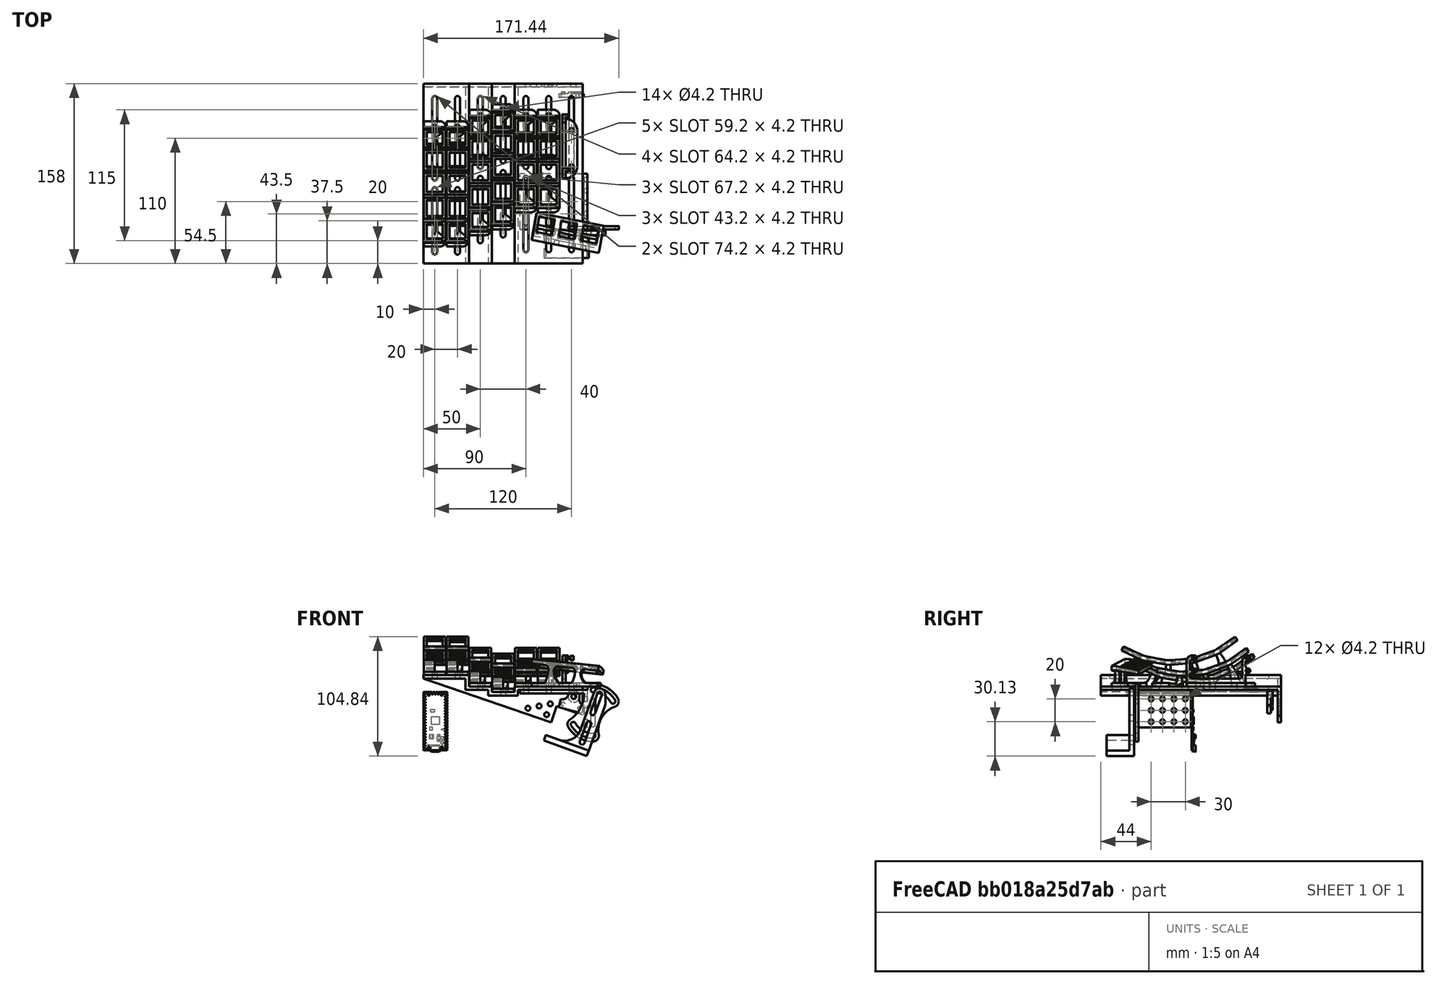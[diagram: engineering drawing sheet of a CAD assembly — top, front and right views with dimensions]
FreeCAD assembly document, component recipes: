
FREECAD ASSEMBLY — COMPONENT RECIPES ("Dactyl Chimera V3")

This assembly document has 15 components, labeled P0..P14 below (a component is one placed body or linked part). 14 of them carry a construction recipe — the FreeCAD feature program that regenerates the part from scratch, quoted from this document or its linked companion documents; the rest are supplied as boundary geometry only. No exploded tour is included for this assembly.
NOTE — document 4 of 4 of this assembly tour. The two overview renders and the header above are repeated from document 1; the component sections below continue where the previous document stopped.
COMPONENT P7 — recipe-attached ("Thumb Cluster", modeled in this document).
Construction recipe (the document's own serialized feature program — sketch geometry with constraints, then the solid features built on it; lengths are millimeters unless a unit is written):

FEATURE [Sketcher::SketchObject] Sketch040
  FullyConstrained = true
  MapMode = 5
  Support = -> [XY_Plane010]
  expr: Constraints[34] = <<Spreadsheet>>.NutR
  expr: Constraints[35] = <<Spreadsheet>>.NutR
  expr: Constraints[41] = <<Spreadsheet>>.NutR
  expr: Constraints[71] = <<Spreadsheet>>.ScrewD
  expr: Constraints[74] = <<Spreadsheet>>.NutR
  sketch-geometry (29):
    g0: LineSegment StartX=-29.5 StartY=10 StartZ=0 EndX=29.5 EndY=10 EndZ=0
    g1: LineSegment StartX=29.5 StartY=10 StartZ=0 EndX=29.5 EndY=0 EndZ=0
    g2: LineSegment StartX=29.5 StartY=0 StartZ=0 EndX=-29.5 EndY=0 EndZ=0
    g3: LineSegment StartX=-29.5 StartY=0 StartZ=0 EndX=-29.5 EndY=10 EndZ=0
    g4: LineSegment StartX=-26.6 StartY=5 StartZ=0 EndX=-26.6 EndY=7.1 EndZ=0
    g5: LineSegment StartX=-26.6 StartY=7.1 StartZ=0 EndX=-10.8667 EndY=7.1 EndZ=0
    g6: LineSegment StartX=-10.8667 StartY=7.1 StartZ=0 EndX=-10.8667 EndY=5 EndZ=0
    g7: LineSegment StartX=-12.9667 StartY=2.9 StartZ=0 EndX=-24.5 EndY=2.9 EndZ=0
    g8: GeomPoint X=-24.5 Y=5 Z=0
    g9: LineSegment StartX=-7.86667 StartY=5 StartZ=0 EndX=-7.86667 EndY=7.1 EndZ=0
    g10: LineSegment StartX=-7.86667 StartY=7.1 StartZ=0 EndX=7.86667 EndY=7.1 EndZ=0
    g11: LineSegment StartX=7.86667 StartY=7.1 StartZ=0 EndX=7.86667 EndY=5 EndZ=0
    g12: LineSegment StartX=5.76667 StartY=2.9 StartZ=0 EndX=-5.76667 EndY=2.9 EndZ=0
    g13: GeomPoint X=0 Y=5 Z=0
    g14: LineSegment StartX=10.8667 StartY=5 StartZ=0 EndX=10.8667 EndY=7.1 EndZ=0
    g15: LineSegment StartX=10.8667 StartY=7.1 StartZ=0 EndX=26.6 EndY=7.1 EndZ=0
    g16: LineSegment StartX=26.6 StartY=7.1 StartZ=0 EndX=26.6 EndY=5 EndZ=0
    g17: LineSegment StartX=24.5 StartY=2.9 StartZ=0 EndX=12.9667 EndY=2.9 EndZ=0
    g18: GeomPoint X=24.5 Y=5 Z=0
    g19: LineSegment StartX=-24.5 StartY=5 StartZ=0 EndX=0 EndY=5 EndZ=0
    g20: LineSegment StartX=0 StartY=5 StartZ=0 EndX=24.5 EndY=5 EndZ=0
    g21: LineSegment StartX=24.5 StartY=2.9 StartZ=0 EndX=26.6 EndY=2.9 EndZ=0
    g22: LineSegment StartX=26.6 StartY=2.9 StartZ=0 EndX=26.6 EndY=5 EndZ=0
    g23: ArcOfCircle CenterX=24.5 CenterY=5 CenterZ=0 NormalX=0 NormalY=0 NormalZ=1 AngleXU=0 Radius=2.1 StartAngle=4.71239 EndAngle=6.28319
    g24: ArcOfCircle CenterX=12.9667 CenterY=5 CenterZ=0 NormalX=0 NormalY=0 NormalZ=1 AngleXU=0 Radius=2.1 StartAngle=3.14159 EndAngle=4.71239
    g25: ArcOfCircle CenterX=5.76667 CenterY=5 CenterZ=0 NormalX=0 NormalY=0 NormalZ=1 AngleXU=0 Radius=2.1 StartAngle=4.71239 EndAngle=6.28319
    g26: ArcOfCircle CenterX=-5.76667 CenterY=5 CenterZ=0 NormalX=0 NormalY=0 NormalZ=1 AngleXU=0 Radius=2.1 StartAngle=3.14159 EndAngle=4.71239
    g27: ArcOfCircle CenterX=-12.9667 CenterY=5 CenterZ=0 NormalX=0 NormalY=0 NormalZ=1 AngleXU=0 Radius=2.1 StartAngle=4.71239 EndAngle=6.28319
    g28: ArcOfCircle CenterX=-24.5 CenterY=5 CenterZ=0 NormalX=0 NormalY=0 NormalZ=1 AngleXU=0 Radius=2.1 StartAngle=3.14159 EndAngle=4.71239
  constraints (76):
    c: Coincident(g0,g1)
    c: Coincident(g1,g2)
    c: Coincident(g2,g3)
    c: Coincident(g3,g0)
    c: Horizontal(g2)
    c: Vertical(g1)
    c: Vertical(g3)
    c: Coincident(g4,g5)
    c: Coincident(g5,g6)
    c: Horizontal(g5)
    c: Horizontal(g7)
    c: Vertical(g4)
    c: Vertical(g6)
    c: Coincident(g9,g10)
    c: Coincident(g10,g11)
    c: Horizontal(g10)
    c: Horizontal(g12)
    c: Vertical(g9)
    c: Vertical(g11)
    c: PointOnObject(g13,g-2)
    c: Coincident(g14,g15)
    c: Coincident(g15,g16)
    c: Horizontal(g15)
    c: Horizontal(g17)
    c: Vertical(g14)
    c: Vertical(g16)
    c: Coincident(g19,g8)
    c: Coincident(g19,g13)
    c: Horizontal(g19)
    c: Coincident(g20,g13)
    c: Coincident(g20,g18)
    c: Horizontal(g20)
    c: Equal(g14,g11)
    c: Equal(g9,g6)
    c: DistanceY(g8,g0) = 5
    c: DistanceY(g2,g8) = 5
    c: DistanceX(g6,g9) = 3
    c: DistanceX(g11,g14) = 3
    c: DistanceX(g2,g2) = 59
    c: Equal(g5,g10)
    c: Equal(g15,g10)
    c: DistanceX(g23,g1) = 5
    c: Symmetric(g0,g0,g-2)
    c: PointOnObject(g-1,g2)
    c: PointOnObject(g14,g20)
    c: PointOnObject(g11,g20)
    c: PointOnObject(g6,g19)
    c: PointOnObject(g9,g19)
    c: PointOnObject(g4,g19)
    c: Coincident(g17,g21)
    c: Coincident(g21,g22)
    c: Coincident(g22,g16)
    c: Vertical(g22)
    c: Tangent(g23,g17) = 1.5708
    c: Tangent(g23,g16) = 1.5708
    c: PointOnObject(g25,g20)
    c: Coincident(g25,g11)
    c: PointOnObject(g26,g19)
    c: Coincident(g26,g9)
    c: PointOnObject(g27,g19)
    c: Coincident(g27,g6)
    c: Coincident(g28,g8)
    c: Coincident(g28,g4)
    c: Tangent(g28,g7) = 1.5708
    c: Tangent(g27,g7) = 1.5708
    c: Tangent(g26,g12) = 1.5708
    c: Tangent(g25,g12) = 1.5708
    c: Tangent(g24,g17) = 1.5708
    c: Tangent(g24,g14) = 1.5708
    c: Coincident(g18,g23)
    c: Equal(g7,g12)
    c: DistanceY(g21,g15) = 4.2
    c: Horizontal(g21)
    c: Equal(g22,g16)
    c: DistanceX(g2,g28) = 5
    c: Horizontal(g17,g12)
FEATURE [PartDesign::Pad] Pad026
  Direction = (0,0,1)
  Length = 3
  Length2 = 10
  Profile = -> Sketch040
  ReferenceAxis = -> Sketch040 [N_Axis]
  Type = 0
FEATURE [PartDesign::Line] DatumLine
  AttacherType = Attacher::AttachEngineLine
  AttachmentOffset = pos=(21,0,0) rot=(0,-1,0;0.10472rad)
  Length = 20
  MapMode = 16
  Placement = pos=(4.7e-15,-4.7e-15,21) rot=(0.743145,0,0.669131;3.14159rad)
  ResizeMode = 0
  Support = -> [XZ_Plane010]
FEATURE [Sketcher::SketchObject] Sketch041
  ExternalGeometry = -> [Sketch040,DatumLine]
  FullyConstrained = true
  MapMode = 5
  Placement = pos=(0,0,0) rot=(1,0,0;1.5708rad)
  Support = -> [XZ_Plane010]
  sketch-geometry (30):
    g0: LineSegment StartX=29.5 StartY=0 StartZ=0 EndX=29.5 EndY=3 EndZ=0
    g1: LineSegment StartX=29.5 StartY=3 StartZ=0 EndX=17.9014 EndY=3 EndZ=0
    g2: LineSegment StartX=-29.5 StartY=0 StartZ=0 EndX=-29.5 EndY=3 EndZ=0
    g3: LineSegment StartX=-29.5 StartY=3 StartZ=0 EndX=-17.9014 EndY=3 EndZ=0
    g4: ArcOfCircle CenterX=-56.761 CenterY=19.4384 CenterZ=0 NormalX=0 NormalY=0 NormalZ=1 AngleXU=0 Radius=42.1934 StartAngle=5.88299 EndAngle=6.17847
    g5: ArcOfCircle CenterX=-14.7725 CenterY=15.0252 CenterZ=0 NormalX=0 NormalY=0 NormalZ=1 AngleXU=0 Radius=23.9737 StartAngle=5.75774 EndAngle=6.17847
    g6: ArcOfCircle CenterX=4.78187 CenterY=12.9699 CenterZ=0 NormalX=0 NormalY=0 NormalZ=1 AngleXU=0 Radius=14.6609 StartAngle=3.03687 EndAngle=3.88941
    g7: ArcOfCircle CenterX=5.60272 CenterY=12.8837 CenterZ=0 NormalX=0 NormalY=0 NormalZ=1 AngleXU=0 Radius=3.48623 StartAngle=6.17847 EndAngle=7.74926
    g8: ArcOfCircle CenterX=-6.33154 CenterY=14.138 CenterZ=0 NormalX=0 NormalY=0 NormalZ=1 AngleXU=0 Radius=3.48623 StartAngle=1.46608 EndAngle=3.03687
    g9: ArcOfCircle CenterX=-18.2658 CenterY=15.3923 CenterZ=0 NormalX=0 NormalY=0 NormalZ=1 AngleXU=0 Radius=3.48623 StartAngle=6.17847 EndAngle=7.74926
    g10: ArcOfCircle CenterX=17.537 CenterY=11.6293 CenterZ=0 NormalX=0 NormalY=0 NormalZ=1 AngleXU=0 Radius=3.48623 StartAngle=1.46608 EndAngle=3.03687
    g11: LineSegment StartX=30.2538 StartY=17.8202 StartZ=0 EndX=-29.4175 EndY=24.0919 EndZ=0
    g12: LineSegment StartX=-29.4175 StartY=24.0919 StartZ=0 EndX=-29.8357 EndY=20.1138 EndZ=0
    g13: LineSegment StartX=-29.8357 StartY=20.1138 StartZ=0 EndX=-17.9014 EndY=18.8595 EndZ=0
    g14: LineSegment StartX=-5.96713 StartY=17.6051 StartZ=0 EndX=5.96713 EndY=16.3508 EndZ=0
    g15: LineSegment StartX=-5.96713 StartY=3 StartZ=0 EndX=5.96713 EndY=3 EndZ=0
    g16: LineSegment StartX=-17.9014 StartY=3 StartZ=0 EndX=-5.96713 EndY=3 EndZ=0
    g17: LineSegment StartX=5.96713 StartY=3 StartZ=0 EndX=17.9014 EndY=3 EndZ=0
    g18: LineSegment StartX=17.9014 StartY=15.0965 StartZ=0 EndX=5.96713 EndY=16.3508 EndZ=0
    g19: LineSegment StartX=-5.96713 StartY=17.6051 StartZ=0 EndX=-17.9014 EndY=18.8595 EndZ=0
    g20: LineSegment StartX=17.9014 StartY=3 StartZ=0 EndX=17.9014 EndY=15.0965 EndZ=0
    g21: LineSegment StartX=5.96713 StartY=3 StartZ=0 EndX=5.96713 EndY=16.3508 EndZ=0
    g22: LineSegment StartX=-5.96713 StartY=17.6051 StartZ=0 EndX=-5.96713 EndY=3 EndZ=0
    g23: LineSegment StartX=-17.9014 StartY=3 StartZ=0 EndX=-17.9014 EndY=18.8595 EndZ=0
    g24: LineSegment StartX=29.5 StartY=0 StartZ=0 EndX=-29.5 EndY=0 EndZ=0
    g25: LineSegment StartX=17.9014 StartY=15.0965 StartZ=0 EndX=29.8357 EndY=13.8421 EndZ=0
    g26: LineSegment StartX=-14.7987 StartY=15.0279 StartZ=0 EndX=14.0699 EndY=11.9937 EndZ=0
    g27: ArcOfCircle CenterX=24.0732 CenterY=10.9423 CenterZ=0 NormalX=0 NormalY=0 NormalZ=1 AngleXU=0 Radius=10.0584 StartAngle=3.03687 EndAngle=4.05179
    g28: LineSegment StartX=29.8357 StartY=13.8421 StartZ=0 EndX=30.2538 EndY=17.8202 EndZ=0
    g29: LineSegment StartX=29.8357 StartY=13.8421 StartZ=0 EndX=28.3808 EndY=0 EndZ=0
  constraints (78):
    c: Coincident(g-3,g0)
    c: Coincident(g0,g1)
    c: Horizontal(g1)
    c: Coincident(g-3,g2)
    c: Vertical(g2)
    c: Coincident(g2,g3)
    c: Horizontal(g3)
    c: Coincident(g11,g12)
    c: Coincident(g12,g13)
    c: Tangent(g14,g8) = 1.5708
    c: Tangent(g8,g6) = -1.5708
    c: Coincident(g15,g6)
    c: Coincident(g15,g5)
    c: Coincident(g16,g6)
    c: Coincident(g17,g5)
    c: Coincident(g17,g1)
    c: Coincident(g18,g7)
    c: Coincident(g19,g13)
    c: Tangent(g9,g13) = 1.5708
    c: Coincident(g10,g26) = -1.5708
    c: Tangent(g7,g5) = -1.5708
    c: Horizontal(g15)
    c: Horizontal(g16)
    c: Horizontal(g17)
    c: Equal(g17,g16)
    c: Equal(g19,g18)
    c: Tangent(g9,g4) = -1.5708
    c: Coincident(g20,g1)
    c: Coincident(g20,g10)
    c: Coincident(g21,g5)
    c: Coincident(g22,g8)
    c: Coincident(g22,g6)
    c: Coincident(g23,g3)
    c: Coincident(g23,g9)
    c: Tangent(g8,g19) = -1.5708
    c: Coincident(g7,g21)
    c: Coincident(g3,g4)
    c: Coincident(g3,g16)
    c: Tangent(g14,g7) = 1.5708
    c: Tangent(g18,g10) = -1.5708
    c: DistanceY(g2,g2) = 3
    c: Equal(g13,g14)
    c: Vertical(g0)
    c: Coincident(g24,g0)
    c: Coincident(g24,g2)
    c: Coincident(g25,g10)
    c: Parallel(g18,g25)
    c: Parallel(g14,g18)
    c: Parallel(g13,g19)
    c: Perpendicular(g11,g12)
    c: Distance(g12) = 4
    c: Vertical(g21)
    c: Vertical(g22)
    c: Vertical(g23)
    c: Equal(g14,g25)
    c: Coincident(g26,g4)
    c: PointOnObject(g6,g26)
    c: PointOnObject(g5,g26)
    c: PointOnObject(g7,g26)
    c: PointOnObject(g8,g26)
    c: Equal(g1,g3)
    c: Distance(g11) = 60
    c: Parallel(g26,g14)
    c: Equal(g25,g18)
    c: PointOnObject(g10,g26)
    c: PointOnObject(g11,g-4)
    c: PointOnObject(g11,g-4)
    c: Coincident(g27,g1)
    c: Tangent(g27,g10) = -1.5708
    c: PointOnObject(g9,g26)
    c: DistanceX(g5,g10) = 5
    c: Coincident(g28,g25)
    c: Coincident(g28,g11)
    c: Coincident(g29,g25)
    c: PointOnObject(g29,g-1)
    c: Angle(g29,g28) = 3.14159
    c: Perpendicular(g28,g25)
    c: Equal(g28,g12)
FEATURE [PartDesign::Pad] Pad027
  BaseFeature = -> Pad026
  Direction = (0,-1,-2e-16)
  Length = 4
  Length2 = 10
  Profile = -> Sketch041
  ReferenceAxis = -> Sketch041 [N_Axis]
  Type = 0
FEATURE [PartDesign::Plane] DatumPlane
  Length = 66.6324
  MapMode = 2
  Placement = pos=(4e-15,-4.7e-15,21) rot=(0.743145,0,0.669131;3.14159rad)
  ResizeMode = 0
  Support = -> [DatumLine]
  Width = 60.5873
FEATURE [Sketcher::SketchObject] Sketch042
  FullyConstrained = true
  MapMode = 5
  Placement = pos=(4.4e-15,-4.7e-15,21) rot=(0.743145,0,0.669131;3.14159rad)
  Support = -> [DatumPlane]
  sketch-geometry (7):
    g0: LineSegment StartX=-3.53373 StartY=-20.3907 StartZ=0 EndX=-7.47296 EndY=-19.6962 EndZ=0
    g1: LineSegment StartX=-7.47296 StartY=-19.6962 StartZ=0 EndX=-4 EndY=0 EndZ=0
    g2: ArcOfCircle CenterX=-4 CenterY=0 CenterZ=0 NormalX=0 NormalY=0 NormalZ=1 AngleXU=0 Radius=4 StartAngle=6.10865 EndAngle=6.95832
    g3: LineSegment StartX=-0.877501 StartY=2.5 StartZ=0 EndX=-4 EndY=0 EndZ=0
    g4: LineSegment StartX=-0.060769 StartY=-0.694593 StartZ=0 EndX=-1.79725 EndY=-10.5427 EndZ=0
    g5: LineSegment StartX=-1.79725 StartY=-10.5427 StartZ=0 EndX=-3.53373 EndY=-20.3907 EndZ=0
    g6: LineSegment StartX=-4 StartY=0 StartZ=0 EndX=-0.060769 EndY=-0.694593 EndZ=0
  constraints (20):
    c: Coincident(g5,g0)
    c: Coincident(g0,g1)
    c: Distance(g0) = 4
    c: Distance(g1) = 20
    c: Perpendicular(g1,g0)
    c: PointOnObject(g1,g-1)
    c: DistanceX(g1,g-1) = 4
    c: Coincident(g2,g1)
    c: Coincident(g2,g4)
    c: Coincident(g3,g2)
    c: Coincident(g3,g1)
    c: DistanceY(g-1,g2) = 2.5
    c: Coincident(g4,g5)
    c: Perpendicular(g4,g0)
    c: Perpendicular(g5,g0)
    c: Equal(g4,g5)
    c: Coincident(g6,g1)
    c: Coincident(g6,g2)
    c: Perpendicular(g1,g6)
    c: Angle(g4,g-1) = 1.74533
FEATURE [PartDesign::Pad] Pad028
  BaseFeature = -> Pad027
  Direction = (0.994522,0,-0.104528)
  Length = 59
  Length2 = 10
  Midplane = true
  Profile = -> Sketch042
  ReferenceAxis = -> Sketch042 [N_Axis]
  Type = 3
  UpToFace = -> Pad027 [Face35]
FEATURE [PartDesign::Pad] Pad029
  BaseFeature = -> Pad028
  Direction = (0.994522,0,-0.104528)
  Length = 10
  Length2 = 10
  Profile = -> Sketch042
  ReferenceAxis = -> Sketch042 [N_Axis]
  Type = 3
  UpToFace = -> Pad028 [Face41]
FEATURE [PartDesign::Plane] DatumPlane001
  AttachmentOffset = pos=(0,0,-20) rot=(0,0,1;0rad)
  Length = 66.6324
  MapMode = 5
  Placement = pos=(-19.8904,-5.1e-15,23.0906) rot=(0.743145,0,0.669131;3.14159rad)
  ResizeMode = 0
  Support = -> [DatumPlane]
  Width = 60.5873
FEATURE [PartDesign::Plane] DatumPlane002
  AttachmentOffset = pos=(0,0,20) rot=(0,0,1;0rad)
  Length = 66.6324
  MapMode = 5
  Placement = pos=(19.8904,-4.2e-15,18.9094) rot=(0.743145,0,0.669131;3.14159rad)
  ResizeMode = 0
  Support = -> [DatumPlane]
  Width = 60.5873
FEATURE [Sketcher::SketchObject] Sketch045
  ExternalGeometry = -> [Sketch042]
  FullyConstrained = true
  MapMode = 5
  Placement = pos=(-19.8904,-5.1e-15,23.0906) rot=(0.743145,0,0.669131;3.14159rad)
  Support = -> [DatumPlane001]
  sketch-geometry (15):
    g0: LineSegment StartX=-1.79725 StartY=-10.5427 StartZ=0 EndX=-3.01279 EndY=-17.4363 EndZ=0
    g1: LineSegment StartX=-3.01279 StartY=-17.4363 StartZ=0 EndX=-4.39152 EndY=-17.1932 EndZ=0
    g2: LineSegment StartX=-4.39152 StartY=-17.1932 StartZ=0 EndX=-4.61726 EndY=-18.4735 EndZ=0
    g3: LineSegment StartX=-4.61726 StartY=-18.4735 StartZ=0 EndX=-7.17776 EndY=-18.022 EndZ=0
    g4: LineSegment StartX=-0.581714 StartY=-3.64902 StartZ=0 EndX=-1.79725 EndY=-10.5427 EndZ=0
    g5: LineSegment StartX=-4.39152 StartY=-17.1932 StartZ=0 EndX=-6.95202 EndY=-16.7417 EndZ=0
    g6: LineSegment StartX=-4.61726 StartY=-18.4735 StartZ=0 EndX=-3.23853 EndY=-18.7166 EndZ=0
    g7: LineSegment StartX=-4.2952 StartY=-1.67417 StartZ=0 EndX=-1.7347 EndY=-2.12566 EndZ=0
    g8: LineSegment StartX=-1.7347 StartY=-2.12566 StartZ=0 EndX=-1.96044 EndY=-3.40591 EndZ=0
    g9: LineSegment StartX=-1.96044 StartY=-3.40591 StartZ=0 EndX=-0.581714 EndY=-3.64902 EndZ=0
    g10: LineSegment StartX=-1.7347 StartY=-2.12566 StartZ=0 EndX=-0.355971 EndY=-2.36877 EndZ=0
    g11: LineSegment StartX=-1.96044 StartY=-3.40591 StartZ=0 EndX=-4.52094 EndY=-2.95442 EndZ=0
    g12: LineSegment StartX=-7.17776 StartY=-18.022 StartZ=0 EndX=-5.73648 EndY=-9.84808 EndZ=0
    g13: LineSegment StartX=-5.73648 StartY=-9.84808 StartZ=0 EndX=-4.2952 EndY=-1.67417 EndZ=0
    g14: LineSegment StartX=-1.79725 StartY=-10.5427 StartZ=0 EndX=-5.73648 EndY=-9.84808 EndZ=0
  constraints (43):
    c: Coincident(g-4,g0)
    c: PointOnObject(g0,g-4)
    c: Coincident(g0,g1)
    c: Coincident(g1,g2)
    c: Coincident(g2,g3)
    c: PointOnObject(g3,g-5)
    c: PointOnObject(g7,g-5)
    c: PointOnObject(g4,g-3)
    c: Coincident(g4,g0)
    c: Equal(g4,g0)
    c: Coincident(g5,g1)
    c: Coincident(g6,g2)
    c: PointOnObject(g6,g-4)
    c: Coincident(g7,g8)
    c: Coincident(g8,g9)
    c: Coincident(g9,g4)
    c: Coincident(g10,g7)
    c: PointOnObject(g10,g-3)
    c: Coincident(g11,g8)
    c: Angle(g9,g11) = 3.14159
    c: Angle(g7,g10) = 3.14159
    c: Angle(g5,g1) = 3.14159
    c: Angle(g6,g3) = 3.14159
    c: Perpendicular(g0,g1)
    c: Perpendicular(g4,g9)
    c: Distance(g0,g4) = 14
    c: Distance(g1) = 1.4
    c: Coincident(g3,g12)
    c: PointOnObject(g12,g-5)
    c: Coincident(g12,g13)
    c: Coincident(g13,g7)
    c: Coincident(g14,g0)
    c: Coincident(g14,g12)
    c: Perpendicular(g4,g14)
    c: Equal(g13,g12)
    c: Distance(g3,g7) = 16.6
    c: Equal(g10,g9)
    c: Equal(g9,g1)
    c: Equal(g1,g6)
    c: PointOnObject(g5,g12)
    c: Perpendicular(g12,g3)
    c: Perpendicular(g13,g7)
    c: PointOnObject(g11,g13)
FEATURE [PartDesign::Pocket] Pocket012
  BaseFeature = -> Pad029
  Direction = (-0.994522,0,0.104528)
  Length = 14
  Length2 = 5
  Midplane = true
  Profile = -> Sketch045
  ReferenceAxis = -> Sketch045 [N_Axis]
  Type = 0
FEATURE [Sketcher::SketchObject] Sketch046
  ExternalGeometry = -> [Sketch042]
  FullyConstrained = true
  MapMode = 5
  Placement = pos=(4.4e-15,-4.7e-15,21) rot=(0.743145,0,0.669131;3.14159rad)
  Support = -> [DatumPlane]
  sketch-geometry (15):
    g0: LineSegment StartX=-0.581714 StartY=-3.64902 StartZ=0 EndX=-1.79725 EndY=-10.5427 EndZ=0
    g1: LineSegment StartX=-1.79725 StartY=-10.5427 StartZ=0 EndX=-3.01279 EndY=-17.4363 EndZ=0
    g2: LineSegment StartX=-3.01279 StartY=-17.4363 StartZ=0 EndX=-4.39152 EndY=-17.1932 EndZ=0
    g3: LineSegment StartX=-4.39152 StartY=-17.1932 StartZ=0 EndX=-4.61726 EndY=-18.4735 EndZ=0
    g4: LineSegment StartX=-4.61726 StartY=-18.4735 StartZ=0 EndX=-7.17776 EndY=-18.022 EndZ=0
    g5: LineSegment StartX=-7.17776 StartY=-18.022 StartZ=0 EndX=-5.73648 EndY=-9.84808 EndZ=0
    g6: LineSegment StartX=-5.73648 StartY=-9.84808 StartZ=0 EndX=-4.2952 EndY=-1.67417 EndZ=0
    g7: LineSegment StartX=-4.2952 StartY=-1.67417 StartZ=0 EndX=-1.7347 EndY=-2.12566 EndZ=0
    g8: LineSegment StartX=-1.7347 StartY=-2.12566 StartZ=0 EndX=-1.96044 EndY=-3.40591 EndZ=0
    g9: LineSegment StartX=-1.96044 StartY=-3.40591 StartZ=0 EndX=-0.581714 EndY=-3.64902 EndZ=0
    g10: LineSegment StartX=-1.7347 StartY=-2.12566 StartZ=0 EndX=-0.355971 EndY=-2.36877 EndZ=0
    g11: LineSegment StartX=-1.96044 StartY=-3.40591 StartZ=0 EndX=-4.52094 EndY=-2.95442 EndZ=0
    g12: LineSegment StartX=-4.39152 StartY=-17.1932 StartZ=0 EndX=-6.95202 EndY=-16.7417 EndZ=0
    g13: LineSegment StartX=-4.61726 StartY=-18.4735 StartZ=0 EndX=-3.23853 EndY=-18.7166 EndZ=0
    g14: LineSegment StartX=-1.79725 StartY=-10.5427 StartZ=0 EndX=-5.73648 EndY=-9.84808 EndZ=0
  constraints (43):
    c: PointOnObject(g0,g-3)
    c: Coincident(g0,g-4)
    c: Coincident(g0,g1)
    c: Coincident(g1,g2)
    c: Coincident(g2,g3)
    c: Coincident(g3,g4)
    c: PointOnObject(g4,g-5)
    c: Coincident(g4,g5)
    c: PointOnObject(g5,g-5)
    c: Coincident(g5,g6)
    c: PointOnObject(g6,g-5)
    c: Coincident(g6,g7)
    c: Coincident(g7,g8)
    c: Coincident(g8,g9)
    c: Coincident(g9,g0)
    c: Coincident(g10,g7)
    c: PointOnObject(g10,g-3)
    c: Coincident(g11,g8)
    c: PointOnObject(g11,g6)
    c: Coincident(g12,g2)
    c: PointOnObject(g12,g5)
    c: Coincident(g13,g3)
    c: PointOnObject(g13,g-4)
    c: Angle(g2,g12) = 3.14159
    c: Angle(g4,g13) = 3.14159
    c: Angle(g9,g11) = 3.14159
    c: Angle(g10,g7) = 3.14159
    c: Equal(g10,g9)
    c: Equal(g9,g2)
    c: Equal(g2,g13)
    c: PointOnObject(g1,g-4)
    c: Coincident(g14,g0)
    c: Coincident(g14,g5)
    c: Perpendicular(g0,g14)
    c: Equal(g0,g1)
    c: Equal(g6,g5)
    c: Distance(g6,g4) = 16.6
    c: Distance(g0,g1) = 14
    c: Perpendicular(g1,g2)
    c: Perpendicular(g9,g0)
    c: Perpendicular(g6,g7)
    c: Distance(g2) = 1.4
    c: Perpendicular(g5,g4)
FEATURE [PartDesign::Pocket] Pocket013
  BaseFeature = -> Pocket012
  Direction = (-0.994522,0,0.104528)
  Length = 14
  Length2 = 5
  Midplane = true
  Profile = -> Sketch046
  ReferenceAxis = -> Sketch046 [N_Axis]
  Type = 0
FEATURE [Sketcher::SketchObject] Sketch047
  ExternalGeometry = -> [Sketch042]
  FullyConstrained = true
  MapMode = 5
  Placement = pos=(19.8904,-4.2e-15,18.9094) rot=(0.743145,0,0.669131;3.14159rad)
  Support = -> [DatumPlane002]
  sketch-geometry (15):
    g0: LineSegment StartX=-0.355971 StartY=-2.36877 StartZ=0 EndX=-1.7347 EndY=-2.12566 EndZ=0
    g1: LineSegment StartX=-3.23853 StartY=-18.7166 StartZ=0 EndX=-4.61726 EndY=-18.4735 EndZ=0
    g2: LineSegment StartX=-6.95202 StartY=-16.7417 StartZ=0 EndX=-4.39152 EndY=-17.1932 EndZ=0
    g3: LineSegment StartX=-4.52094 StartY=-2.95442 StartZ=0 EndX=-1.96044 EndY=-3.40591 EndZ=0
    g4: LineSegment StartX=-4.2952 StartY=-1.67417 StartZ=0 EndX=-1.7347 EndY=-2.12566 EndZ=0
    g5: LineSegment StartX=-1.7347 StartY=-2.12566 StartZ=0 EndX=-1.96044 EndY=-3.40591 EndZ=0
    g6: LineSegment StartX=-1.96044 StartY=-3.40591 StartZ=0 EndX=-0.581714 EndY=-3.64902 EndZ=0
    g7: LineSegment StartX=-0.581714 StartY=-3.64902 StartZ=0 EndX=-1.79725 EndY=-10.5427 EndZ=0
    g8: LineSegment StartX=-1.79725 StartY=-10.5427 StartZ=0 EndX=-3.01279 EndY=-17.4363 EndZ=0
    g9: LineSegment StartX=-3.01279 StartY=-17.4363 StartZ=0 EndX=-4.39152 EndY=-17.1932 EndZ=0
    g10: LineSegment StartX=-4.39152 StartY=-17.1932 StartZ=0 EndX=-4.61726 EndY=-18.4735 EndZ=0
    g11: LineSegment StartX=-4.61726 StartY=-18.4735 StartZ=0 EndX=-7.17776 EndY=-18.022 EndZ=0
    g12: LineSegment StartX=-7.17776 StartY=-18.022 StartZ=0 EndX=-5.73648 EndY=-9.84808 EndZ=0
    g13: LineSegment StartX=-5.73648 StartY=-9.84808 StartZ=0 EndX=-4.2952 EndY=-1.67417 EndZ=0
    g14: LineSegment StartX=-1.79725 StartY=-10.5427 StartZ=0 EndX=-5.73648 EndY=-9.84808 EndZ=0
  constraints (43):
    c: PointOnObject(g0,g-3)
    c: PointOnObject(g1,g-4)
    c: PointOnObject(g2,g-5)
    c: PointOnObject(g3,g-5)
    c: PointOnObject(g4,g-5)
    c: Coincident(g4,g0)
    c: Coincident(g4,g5)
    c: Coincident(g5,g3)
    c: Coincident(g5,g6)
    c: PointOnObject(g6,g-3)
    c: Coincident(g6,g7)
    c: Coincident(g7,g-4)
    c: Coincident(g7,g8)
    c: PointOnObject(g8,g-4)
    c: Coincident(g8,g9)
    c: Coincident(g9,g2)
    c: Coincident(g9,g10)
    c: Coincident(g10,g1)
    c: Coincident(g10,g11)
    c: Coincident(g11,g12)
    c: PointOnObject(g12,g-5)
    c: Coincident(g12,g13)
    c: Coincident(g13,g4)
    c: Perpendicular(g7,g6)
    c: Perpendicular(g13,g4)
    c: Perpendicular(g8,g9)
    c: Perpendicular(g12,g11)
    c: PointOnObject(g11,g-5)
    c: Coincident(g14,g7)
    c: Coincident(g14,g12)
    c: Perpendicular(g7,g14)
    c: Angle(g3,g6) = 3.14159
    c: Angle(g0,g4) = 3.14159
    c: Angle(g2,g9) = 3.14159
    c: Angle(g1,g11) = 3.14159
    c: Equal(g1,g9)
    c: Equal(g9,g6)
    c: Equal(g6,g0)
    c: Distance(g6) = 1.4
    c: Equal(g8,g7)
    c: Equal(g13,g12)
    c: Distance(g8,g6) = 14
    c: Distance(g4,g11) = 16.6
FEATURE [PartDesign::Pocket] Pocket014
  BaseFeature = -> Pocket013
  Direction = (-0.994522,0,0.104528)
  Length = 14
  Length2 = 5
  Midplane = true
  Profile = -> Sketch047
  ReferenceAxis = -> Sketch047 [N_Axis]
  Type = 0
FEATURE [Sketcher::SketchObject] Sketch062
  ExternalGeometry = -> [Sketch046]
  FullyConstrained = true
  MapMode = 5
  Placement = pos=(4.4e-15,-4.7e-15,21) rot=(0.743145,0,0.669131;3.14159rad)
  Support = -> [DatumPlane]
  sketch-geometry (11):
    g0: LineSegment StartX=-1.79725 StartY=-10.5427 StartZ=0 EndX=-2.97902 EndY=-10.3343 EndZ=0
    g1: LineSegment StartX=-2.97902 StartY=-10.3343 StartZ=0 EndX=-3.96383 EndY=-10.1606 EndZ=0
    g2: LineSegment StartX=-3.96383 StartY=-10.1606 StartZ=0 EndX=-5.73648 EndY=-9.84808 EndZ=0
    g3: LineSegment StartX=-4.19456 StartY=-17.2279 StartZ=0 EndX=-1.76348 EndY=-3.44064 EndZ=0
    g4: LineSegment StartX=-1.76348 StartY=-3.44064 StartZ=0 EndX=-1.96044 EndY=-3.40591 EndZ=0
    g5: LineSegment StartX=-1.96044 StartY=-3.40591 StartZ=0 EndX=-1.7347 EndY=-2.12566 EndZ=0
    g6: LineSegment StartX=-1.7347 StartY=-2.12566 StartZ=0 EndX=-2.52255 EndY=-1.98674 EndZ=0
    g7: LineSegment StartX=-2.52255 StartY=-1.98674 StartZ=0 EndX=-5.40511 EndY=-18.3345 EndZ=0
    g8: LineSegment StartX=-5.40511 StartY=-18.3345 StartZ=0 EndX=-4.61726 EndY=-18.4735 EndZ=0
    g9: LineSegment StartX=-4.61726 StartY=-18.4735 StartZ=0 EndX=-4.39152 EndY=-17.1932 EndZ=0
    g10: LineSegment StartX=-4.39152 StartY=-17.1932 StartZ=0 EndX=-4.19456 EndY=-17.2279 EndZ=0
  constraints (28):
    c: Coincident(g-3,g0)
    c: Coincident(g0,g1)
    c: Coincident(g1,g2)
    c: Coincident(g2,g-4)
    c: Angle(g1,g2) = 3.14159
    c: Angle(g1,g0) = 3.14159
    c: Distance(g0) = 1.2
    c: Distance(g1) = 1
    c: PointOnObject(g3,g-5)
    c: PointOnObject(g3,g-8)
    c: Coincident(g3,g4)
    c: Coincident(g4,g-8)
    c: Coincident(g4,g5)
    c: Coincident(g5,g-7)
    c: Coincident(g5,g6)
    c: PointOnObject(g6,g-7)
    c: Coincident(g6,g7)
    c: PointOnObject(g7,g-6)
    c: Coincident(g7,g8)
    c: Coincident(g8,g-6)
    c: Coincident(g8,g9)
    c: Coincident(g9,g-5)
    c: Coincident(g9,g10)
    c: Coincident(g10,g3)
    c: PointOnObject(g0,g3)
    c: PointOnObject(g1,g7)
    c: Perpendicular(g7,g1)
    c: Perpendicular(g0,g3)
FEATURE [PartDesign::Pocket] Pocket020
  BaseFeature = -> Pocket014
  Direction = (-0.994522,0,0.104528)
  Length = 14.6
  Length2 = 5
  Midplane = true
  Profile = -> Sketch062
  ReferenceAxis = -> Sketch062 [N_Axis]
  Type = 0
FEATURE [Sketcher::SketchObject] Sketch063
  ExternalGeometry = -> [Sketch045]
  FullyConstrained = true
  MapMode = 5
  Placement = pos=(-19.8904,-5.1e-15,23.0906) rot=(0.743145,0,0.669131;3.14159rad)
  Support = -> [DatumPlane001]
  sketch-geometry (11):
    g0: LineSegment StartX=-1.76348 StartY=-3.44064 StartZ=0 EndX=-4.19456 EndY=-17.2279 EndZ=0
    g1: LineSegment StartX=-4.19456 StartY=-17.2279 StartZ=0 EndX=-4.39152 EndY=-17.1932 EndZ=0
    g2: LineSegment StartX=-4.39152 StartY=-17.1932 StartZ=0 EndX=-4.61726 EndY=-18.4735 EndZ=0
    g3: LineSegment StartX=-4.61726 StartY=-18.4735 StartZ=0 EndX=-5.40511 EndY=-18.3345 EndZ=0
    g4: LineSegment StartX=-5.40511 StartY=-18.3345 StartZ=0 EndX=-2.52255 EndY=-1.98674 EndZ=0
    g5: LineSegment StartX=-2.52255 StartY=-1.98674 StartZ=0 EndX=-1.7347 EndY=-2.12566 EndZ=0
    g6: LineSegment StartX=-1.7347 StartY=-2.12566 StartZ=0 EndX=-1.96044 EndY=-3.40591 EndZ=0
    g7: LineSegment StartX=-1.96044 StartY=-3.40591 StartZ=0 EndX=-1.76348 EndY=-3.44064 EndZ=0
    g8: LineSegment StartX=-1.79725 StartY=-10.5427 StartZ=0 EndX=-2.97902 EndY=-10.3343 EndZ=0
    g9: LineSegment StartX=-2.97902 StartY=-10.3343 StartZ=0 EndX=-3.96383 EndY=-10.1606 EndZ=0
    g10: LineSegment StartX=-3.96383 StartY=-10.1606 StartZ=0 EndX=-5.73648 EndY=-9.84808 EndZ=0
  constraints (28):
    c: PointOnObject(g0,g-7)
    c: PointOnObject(g0,g-3)
    c: Coincident(g0,g1)
    c: Coincident(g1,g-3)
    c: Coincident(g1,g2)
    c: Coincident(g2,g-4)
    c: Coincident(g2,g3)
    c: PointOnObject(g3,g-4)
    c: Coincident(g3,g4)
    c: PointOnObject(g4,g-8)
    c: Coincident(g4,g5)
    c: Coincident(g5,g-8)
    c: Coincident(g5,g6)
    c: Coincident(g6,g-7)
    c: Coincident(g6,g7)
    c: Coincident(g7,g0)
    c: Coincident(g-6,g8)
    c: PointOnObject(g8,g0)
    c: Coincident(g8,g9)
    c: PointOnObject(g9,g4)
    c: Coincident(g9,g10)
    c: Coincident(g10,g-5)
    c: Angle(g9,g10) = 3.14159
    c: Angle(g9,g8) = 3.14159
    c: Distance(g8) = 1.2
    c: Distance(g9) = 1
    c: Perpendicular(g0,g8)
    c: Perpendicular(g4,g9)
FEATURE [PartDesign::Pocket] Pocket021
  BaseFeature = -> Pocket020
  Direction = (-0.994522,0,0.104528)
  Length = 14.6
  Length2 = 5
  Midplane = true
  Profile = -> Sketch063
  ReferenceAxis = -> Sketch063 [N_Axis]
  Type = 0
FEATURE [Sketcher::SketchObject] Sketch064
  ExternalGeometry = -> [Sketch047]
  FullyConstrained = true
  MapMode = 5
  Placement = pos=(19.8904,-4.2e-15,18.9094) rot=(0.743145,0,0.669131;3.14159rad)
  Support = -> [DatumPlane002]
  sketch-geometry (11):
    g0: LineSegment StartX=-1.76348 StartY=-3.44064 StartZ=0 EndX=-1.96044 EndY=-3.40591 EndZ=0
    g1: LineSegment StartX=-1.96044 StartY=-3.40591 StartZ=0 EndX=-1.7347 EndY=-2.12566 EndZ=0
    g2: LineSegment StartX=-1.7347 StartY=-2.12566 StartZ=0 EndX=-2.52255 EndY=-1.98674 EndZ=0
    g3: LineSegment StartX=-2.52255 StartY=-1.98674 StartZ=0 EndX=-5.40511 EndY=-18.3345 EndZ=0
    g4: LineSegment StartX=-5.40511 StartY=-18.3345 StartZ=0 EndX=-4.61726 EndY=-18.4735 EndZ=0
    g5: LineSegment StartX=-4.61726 StartY=-18.4735 StartZ=0 EndX=-4.39152 EndY=-17.1932 EndZ=0
    g6: LineSegment StartX=-4.39152 StartY=-17.1932 StartZ=0 EndX=-4.19456 EndY=-17.2279 EndZ=0
    g7: LineSegment StartX=-4.19456 StartY=-17.2279 StartZ=0 EndX=-1.76348 EndY=-3.44064 EndZ=0
    g8: LineSegment StartX=-1.79725 StartY=-10.5427 StartZ=0 EndX=-2.97902 EndY=-10.3343 EndZ=0
    g9: LineSegment StartX=-2.97902 StartY=-10.3343 StartZ=0 EndX=-3.96383 EndY=-10.1606 EndZ=0
    g10: LineSegment StartX=-3.96383 StartY=-10.1606 StartZ=0 EndX=-5.73648 EndY=-9.84808 EndZ=0
  constraints (28):
    c: PointOnObject(g0,g-3)
    c: Coincident(g0,g-3)
    c: Coincident(g0,g1)
    c: Coincident(g1,g-4)
    c: Coincident(g1,g2)
    c: PointOnObject(g2,g-4)
    c: Coincident(g2,g3)
    c: PointOnObject(g3,g-6)
    c: Coincident(g3,g4)
    c: Coincident(g4,g-6)
    c: Coincident(g4,g5)
    c: Coincident(g5,g-5)
    c: Coincident(g5,g6)
    c: PointOnObject(g6,g-5)
    c: Coincident(g6,g7)
    c: Coincident(g7,g0)
    c: Coincident(g-8,g8)
    c: PointOnObject(g8,g7)
    c: Coincident(g8,g9)
    c: PointOnObject(g9,g3)
    c: Coincident(g9,g10)
    c: Coincident(g10,g-7)
    c: Angle(g10,g9) = 3.14159
    c: Angle(g8,g9) = 3.14159
    c: Distance(g8) = 1.2
    c: Distance(g9) = 1
    c: Perpendicular(g3,g9)
    c: Perpendicular(g8,g7)
FEATURE [PartDesign::Pocket] Pocket022
  BaseFeature = -> Pocket021
  Direction = (-0.994522,0,0.104528)
  Length = 14.6
  Length2 = 5
  Midplane = true
  Profile = -> Sketch064
  ReferenceAxis = -> Sketch064 [N_Axis]
  Type = 0
FEATURE [PartDesign::Body] Body008  label="Thumb Cluster"
  Group = -> [Sketch040,Pad026,Sketch041,Pad027,DatumLine,DatumPlane,Sketch042,Pad028,Pad029,DatumPlane001,DatumPlane002,Sketch045,Pocket012,Sketch046,Pocket013,Sketch047,Pocket014,Sketch062,Pocket020,Sketch063,Pocket021,Sketch064,Pocket022]
  Origin = -> Origin010
  Placement = pos=(125,-61,5) rot=(0,0,-1;0.191986rad)
  Tip = -> Pocket022
  expr: .Placement.Base.z = <<InnerIndexArch>>.Placement.Base.z
COMPONENT P8 — recipe-attached ("RJ11Holder", modeled in this document).
Construction recipe (the document's own serialized feature program — sketch geometry with constraints, then the solid features built on it; lengths are millimeters unless a unit is written):

FEATURE [Sketcher::SketchObject] Sketch043
  FullyConstrained = true
  MapMode = 5
  Placement = pos=(0,0,0) rot=(1,0,0;1.5708rad)
  Support = -> [XZ_Plane011]
  expr: Constraints[26] = <<Spreadsheet>>.NutR
  expr: Constraints[3] = <<Spreadsheet>>.ScrewD
  expr: Constraints[7] = <<Spreadsheet>>.NutR
  sketch-geometry (13):
    g0: LineSegment StartX=-10.25 StartY=-7.5 StartZ=0 EndX=10.25 EndY=-7.5 EndZ=0
    g1: LineSegment StartX=10.25 StartY=-7.5 StartZ=0 EndX=10.25 EndY=3.83222e-11 EndZ=0
    g2: LineSegment StartX=-10.25 StartY=3.83222e-11 StartZ=0 EndX=-10.25 EndY=-7.5 EndZ=0
    g3: Circle CenterX=0 CenterY=5 CenterZ=0 NormalX=0 NormalY=0 NormalZ=1 AngleXU=0 Radius=2.1
    g4: LineSegment StartX=-10.25 StartY=3.83222e-11 StartZ=0 EndX=10.25 EndY=3.83222e-11 EndZ=0
    g5: Circle CenterX=-7.345 CenterY=-3.75 CenterZ=0 NormalX=0 NormalY=0 NormalZ=1 AngleXU=0 Radius=1.625
    g6: Circle CenterX=7.345 CenterY=-3.75 CenterZ=0 NormalX=0 NormalY=0 NormalZ=1 AngleXU=0 Radius=1.625
    g7: LineSegment StartX=0 StartY=10 StartZ=0 EndX=0 EndY=-7.5 EndZ=0
    g8: LineSegment StartX=-7.345 StartY=-3.75 StartZ=0 EndX=0 EndY=-3.75 EndZ=0
    g9: LineSegment StartX=0 StartY=-3.75 StartZ=0 EndX=7.345 EndY=-3.75 EndZ=0
    g10: ArcOfCircle CenterX=0 CenterY=5 CenterZ=0 NormalX=0 NormalY=0 NormalZ=1 AngleXU=0 Radius=5 StartAngle=0.0246921 EndAngle=3.1169
    g11: ArcOfCircle CenterX=10.25 CenterY=5.25315 CenterZ=0 NormalX=0 NormalY=0 NormalZ=1 AngleXU=0 Radius=5.25315 StartAngle=3.16628 EndAngle=4.71239
    g12: ArcOfCircle CenterX=-10.25 CenterY=5.25315 CenterZ=0 NormalX=0 NormalY=0 NormalZ=1 AngleXU=0 Radius=5.25315 StartAngle=4.71239 EndAngle=6.25849
  constraints (37):
    c: Coincident(g0,g1)
    c: Horizontal(g0)
    c: Vertical(g1)
    c: Diameter(g3) = 4.2
    c: PointOnObject(g4,g2)
    c: Horizontal(g4)
    c: DistanceY(g0,g4) = 7.5
    c: DistanceY(g4,g3) = 5
    c: DistanceX(g0,g0) = 20.5
    c: DistanceX(g5,g6) = 14.69
    c: Diameter(g6) = 3.25
    c: PointOnObject(g7,g0)
    c: Vertical(g7)
    c: Symmetric(g2,g1,g7)
    c: PointOnObject(g3,g7)
    c: Coincident(g8,g5)
    c: PointOnObject(g8,g7)
    c: Horizontal(g8)
    c: Coincident(g8,g9)
    c: Coincident(g9,g6)
    c: Horizontal(g9)
    c: Equal(g9,g8)
    c: Equal(g5,g6)
    c: Symmetric(g4,g0,g8)
    c: Coincident(g10,g3)
    c: PointOnObject(g7,g10)
    c: Radius(g10) = 5
    c: Coincident(g11,g1)
    c: Tangent(g11,g10) = 1.5708
    c: Coincident(g1,g4)
    c: Coincident(g12,g2)
    c: Tangent(g12,g10) = 1.5708
    c: Equal(g12,g11)
    c: Tangent(g11,g4)
    c: Coincident(g2,g0)
    c: PointOnObject(g-1,g7)
    c: PointOnObject(g-1,g4)
FEATURE [PartDesign::Pad] Pad030
  Direction = (0,-1,-2e-16)
  Length = 3
  Length2 = 10
  Placement = pos=(0,0,0) rot=(1,0,0;1.5708rad)
  Profile = -> Sketch043
  ReferenceAxis = -> Sketch043 [N_Axis]
  Reversed = true
  Type = 0
FEATURE [Sketcher::SketchObject] Sketch044
  FullyConstrained = true
  MapMode = 5
  Placement = pos=(0,0,0) rot=(1,0,0;1.5708rad)
  Support = -> [XZ_Plane011]
  expr: Constraints[11] = <<Spreadsheet>>.ScrewD
  expr: Constraints[12] = <<Spreadsheet>>.NutR * 2
  sketch-geometry (6):
    g0: Circle CenterX=7.345 CenterY=-3.75 CenterZ=0 NormalX=0 NormalY=0 NormalZ=1 AngleXU=0 Radius=1.5
    g1: Circle CenterX=-7.345 CenterY=-3.75 CenterZ=0 NormalX=0 NormalY=0 NormalZ=1 AngleXU=0 Radius=1.5
    g2: LineSegment StartX=-7.345 StartY=-3.75 StartZ=0 EndX=7.345 EndY=-3.75 EndZ=0
    g3: LineSegment StartX=0 StartY=0 StartZ=0 EndX=0 EndY=-7.5 EndZ=0
    g4: Circle CenterX=0 CenterY=5 CenterZ=0 NormalX=0 NormalY=0 NormalZ=1 AngleXU=0 Radius=5
    g5: Circle CenterX=0 CenterY=5 CenterZ=0 NormalX=0 NormalY=0 NormalZ=1 AngleXU=0 Radius=2.1
  constraints (14):
    c: Coincident(g2,g1)
    c: Coincident(g2,g0)
    c: Equal(g0,g1)
    c: DistanceX(g2,g2) = 14.69
    c: Diameter(g0) = 3
    c: Symmetric(g1,g0,g-2)
    c: Coincident(g3,g-1)
    c: DistanceY(g3,g3) = 7.5
    c: Symmetric(g3,g3,g2)
    c: PointOnObject(g4,g-2)
    c: Coincident(g5,g4)
    c: Diameter(g5) = 4.2
    c: Diameter(g4) = 10
    c: PointOnObject(g3,g4)
FEATURE [PartDesign::Pad] Pad031
  BaseFeature = -> Pad030
  Direction = (0,-1,-2e-16)
  Length = 1.57
  Length2 = 10
  Placement = pos=(0,0,0) rot=(1,0,0;1.5708rad)
  Profile = -> Sketch044
  ReferenceAxis = -> Sketch044 [N_Axis]
  Type = 0
FEATURE [PartDesign::Body] Body009  label="RJ11Holder"
  Group = -> [Sketch043,Pad030,Sketch044,Pad031]
  Origin = -> Origin011
  Placement = pos=(130.775,69,-8.70711) rot=(0.130526,0,0.991445;3.14159rad)
  Tip = -> Pad031
COMPONENT P9 — recipe-attached ("PicoBase", modeled in this document).
Construction recipe (the document's own serialized feature program — sketch geometry with constraints, then the solid features built on it; lengths are millimeters unless a unit is written):

FEATURE [Sketcher::SketchObject] Sketch049
  FullyConstrained = true
  MapMode = 5
  Placement = pos=(0,0,0) rot=(0.57735,0.57735,0.57735;2.0944rad)
  Support = -> [YZ_Plane012]
  expr: Constraints[88] = <<Spreadsheet>>.Wiring
  sketch-geometry (43):
    g0: Circle CenterX=49 CenterY=13.8 CenterZ=0 NormalX=0 NormalY=0 NormalZ=1 AngleXU=0 Radius=1.1
    g1: Circle CenterX=49 CenterY=25.2 CenterZ=0 NormalX=0 NormalY=0 NormalZ=1 AngleXU=0 Radius=1.1
    g2: Circle CenterX=2 CenterY=25.2 CenterZ=0 NormalX=0 NormalY=0 NormalZ=1 AngleXU=0 Radius=1.1
    g3: Circle CenterX=2 CenterY=13.8 CenterZ=0 NormalX=0 NormalY=0 NormalZ=1 AngleXU=0 Radius=1.1
    g4: ArcOfCircle CenterX=2 CenterY=25.2 CenterZ=0 NormalX=0 NormalY=0 NormalZ=1 AngleXU=0 Radius=2 StartAngle=4.71239 EndAngle=7.85398
    g5: ArcOfCircle CenterX=2 CenterY=13.8 CenterZ=0 NormalX=0 NormalY=0 NormalZ=1 AngleXU=0 Radius=2 StartAngle=4.71239 EndAngle=7.85398
    g6: ArcOfCircle CenterX=49 CenterY=13.8 CenterZ=0 NormalX=0 NormalY=0 NormalZ=1 AngleXU=0 Radius=2 StartAngle=4.71239 EndAngle=7.85398
    g7: ArcOfCircle CenterX=49 CenterY=25.2 CenterZ=0 NormalX=0 NormalY=0 NormalZ=1 AngleXU=0 Radius=2 StartAngle=4.71239 EndAngle=7.85398
    g8: LineSegment StartX=2 StartY=23.2 StartZ=0 EndX=0 EndY=23.2 EndZ=0
    g9: LineSegment StartX=2 StartY=27.2 StartZ=0 EndX=2e-16 EndY=27.2 EndZ=0
    g10: ArcOfCircle CenterX=0 CenterY=21.2 CenterZ=0 NormalX=0 NormalY=0 NormalZ=1 AngleXU=0 Radius=2 StartAngle=1.5708 EndAngle=3.14159
    g11: ArcOfCircle CenterX=0 CenterY=22.2 CenterZ=0 NormalX=0 NormalY=0 NormalZ=1 AngleXU=0 Radius=5 StartAngle=1.5708 EndAngle=3.14159
    g12: LineSegment StartX=-2 StartY=21.2 StartZ=0 EndX=-2 EndY=14.416 EndZ=0
    g13: LineSegment StartX=-5 StartY=22.2 StartZ=0 EndX=-5 EndY=0 EndZ=0
    g14: LineSegment StartX=2 StartY=15.8 StartZ=0 EndX=7e-16 EndY=15.8 EndZ=0
    g15: LineSegment StartX=2 StartY=11.8 StartZ=0 EndX=2e-16 EndY=11.8 EndZ=0
    g16: ArcOfCircle CenterX=0 CenterY=9.4 CenterZ=0 NormalX=0 NormalY=0 NormalZ=1 AngleXU=0 Radius=2.4 StartAngle=1.5708 EndAngle=4.71239
    g17: LineSegment StartX=2 StartY=13.8 StartZ=0 EndX=2 EndY=25.2 EndZ=0
    g18: LineSegment StartX=49 StartY=13.8 StartZ=0 EndX=49 EndY=25.2 EndZ=0
    g19: LineSegment StartX=2 StartY=13.8 StartZ=0 EndX=49 EndY=13.8 EndZ=0
    g20: LineSegment StartX=42 StartY=9 StartZ=0 EndX=42 EndY=30 EndZ=0
    g21: LineSegment StartX=42 StartY=30 StartZ=0 EndX=2 EndY=27.2 EndZ=0
    g22: LineSegment StartX=2 StartY=11.8 StartZ=0 EndX=42 EndY=9 EndZ=0
    g23: LineSegment StartX=42 StartY=9 StartZ=0 EndX=42 EndY=7 EndZ=0
    g24: LineSegment StartX=0 StartY=21.2 StartZ=0 EndX=-2 EndY=21.2 EndZ=0
    g25: LineSegment StartX=0 StartY=7 StartZ=0 EndX=42 EndY=7 EndZ=0
    g26: ArcOfCircle CenterX=42 CenterY=9 CenterZ=0 NormalX=0 NormalY=0 NormalZ=1 AngleXU=0 Radius=2 StartAngle=4.71239 EndAngle=6.28319
    g27: ArcOfCircle CenterX=49 CenterY=17.8 CenterZ=0 NormalX=0 NormalY=0 NormalZ=1 AngleXU=0 Radius=2 StartAngle=3.14159 EndAngle=4.71239
    g28: ArcOfCircle CenterX=49 CenterY=21.2 CenterZ=0 NormalX=0 NormalY=0 NormalZ=1 AngleXU=0 Radius=2 StartAngle=1.5708 EndAngle=3.14159
    g29: LineSegment StartX=47 StartY=21.2 StartZ=0 EndX=47 EndY=17.8 EndZ=0
    g30: ArcOfCircle CenterX=49 CenterY=22.2 CenterZ=0 NormalX=0 NormalY=0 NormalZ=1 AngleXU=0 Radius=5 StartAngle=1.5708 EndAngle=3.14159
    g31: LineSegment StartX=49 StartY=25.2 StartZ=0 EndX=49 EndY=27.2 EndZ=0
    g32: LineSegment StartX=44 StartY=22.2 StartZ=0 EndX=44 EndY=9 EndZ=0
    g33: LineSegment StartX=51 StartY=0 StartZ=0 EndX=51 EndY=3 EndZ=0
    g34: LineSegment StartX=51 StartY=3 StartZ=0 EndX=51 EndY=13.8 EndZ=0
    g35: ArcOfCircle CenterX=2.14e-14 CenterY=13.6629 CenterZ=0 NormalX=0 NormalY=0 NormalZ=1 AngleXU=0 Radius=2.13707 StartAngle=1.5708 EndAngle=2.78149
    g36: LineSegment StartX=-0.888889 StartY=11.6293 StartZ=0 EndX=-2 EndY=14.416 EndZ=0
    g37: ArcOfCircle CenterX=49 CenterY=9.8 CenterZ=0 NormalX=0 NormalY=0 NormalZ=1 AngleXU=0 Radius=2 StartAngle=1.5708 EndAngle=3.14159
    g38: LineSegment StartX=-5 StartY=0 StartZ=0 EndX=47 EndY=0 EndZ=0
    g39: LineSegment StartX=47 StartY=0 StartZ=0 EndX=51 EndY=0 EndZ=0
    g40: LineSegment StartX=47 StartY=9.8 StartZ=0 EndX=47 EndY=0 EndZ=0
    g41: LineSegment StartX=49 StartY=11.8 StartZ=0 EndX=49 EndY=13.8 EndZ=0
    g42: LineSegment StartX=47 StartY=21.2 StartZ=0 EndX=49 EndY=21.2 EndZ=0
  constraints (114):
    c: Diameter(g2) = 2.2
    c: Equal(g3,g2)
    c: Equal(g2,g1)
    c: Equal(g1,g0)
    c: Coincident(g4,g2)
    c: Coincident(g5,g3)
    c: Coincident(g6,g0)
    c: Coincident(g7,g1)
    c: DistanceY(g3,g2) = 11.4
    c: Diameter(g4) = 4
    c: Equal(g4,g5)
    c: Equal(g5,g6)
    c: Equal(g6,g7)
    c: PointOnObject(g39,g-1)
    c: PointOnObject(g8,g-2)
    c: Horizontal(g8)
    c: Tangent(g-2,g4)
    c: Tangent(g4,g8) = 1.5708
    c: PointOnObject(g9,g-2)
    c: Horizontal(g9)
    c: Tangent(g9,g4) = -1.5708
    c: PointOnObject(g10,g-2)
    c: Coincident(g10,g8)
    c: PointOnObject(g11,g-2)
    c: Coincident(g11,g9)
    c: DistanceX(g11,g10) = 3
    c: Vertical(g12)
    c: Tangent(g12,g10) = -1.5708
    c: Vertical(g13)
    c: Tangent(g13,g11) = -1.5708
    c: PointOnObject(g14,g-2)
    c: Horizontal(g14)
    c: Tangent(g5,g14) = -1.5708
    c: PointOnObject(g15,g-2)
    c: Horizontal(g15)
    c: PointOnObject(g16,g-2)
    c: Coincident(g16,g15)
    c: Coincident(g17,g5)
    c: Coincident(g17,g4)
    c: Vertical(g17)
    c: Coincident(g18,g0)
    c: Coincident(g18,g1)
    c: Vertical(g18)
    c: Equal(g18,g17)
    c: Coincident(g19,g5)
    c: Coincident(g19,g0)
    c: Horizontal(g19)
    c: Vertical(g20)
    c: DistanceY(g20,g20) = 21
    c: Coincident(g21,g20)
    c: Coincident(g21,g4)
    c: Coincident(g22,g5)
    c: Coincident(g22,g20)
    c: Tangent(g15,g5) = 1.5708
    c: Equal(g21,g22)
    c: PointOnObject(g16,g-2)
    c: Coincident(g23,g20)
    c: Vertical(g23)
    c: Coincident(g24,g10)
    c: Coincident(g24,g10)
    c: Equal(g24,g23)
    c: Coincident(g25,g16)
    c: Horizontal(g25)
    c: Coincident(g13,g38)
    c: PointOnObject(g38,g-1)
    c: Tangent(g25,g26) = -1.5708
    c: Coincident(g23,g25)
    c: PointOnObject(g6,g18)
    c: PointOnObject(g27,g18)
    c: Coincident(g27,g6)
    c: PointOnObject(g28,g18)
    c: Tangent(g29,g28) = -1.5708
    c: Tangent(g29,g27) = -1.5708
    c: Vertical(g29)
    c: Tangent(g7,g28) = 1.5708
    c: Tangent(g7,g30) = -1.5708
    c: Coincident(g31,g1)
    c: Coincident(g31,g7)
    c: Vertical(g31)
    c: Vertical(g32)
    c: Tangent(g32,g30) = -1.5708
    c: DistanceX(g30,g28) = 3
    c: Tangent(g32,g26) = 1.5708
    c: Coincident(g33,g39)
    c: Vertical(g33)
    c: DistanceY(g33,g33) = 3
    c: Coincident(g34,g33)
    c: Tangent(g34,g6) = -1.5708
    c: DistanceY(g33,g26) = 6
    c: DistanceX(g-1,g39) = 51
    c: Tangent(g35,g14) = -1.5708
    c: Coincident(g35,g12)
    c: PointOnObject(g36,g16)
    c: Coincident(g36,g12)
    c: Perpendicular(g16,g36)
    c: Distance(g36) = 3
    c: Vertical(g34)
    c: DistanceX(g24,g24) = 2
    c: Horizontal(g20,g26)
    c: Coincident(g38,g39)
    c: PointOnObject(g38,g-1)
    c: Vertical(g38,g37)
    c: DistanceX(g26,g37) = 3
    c: Coincident(g40,g38)
    c: Tangent(g40,g37) = -1.5708
    c: Tangent(g37,g6) = 1.5708
    c: Coincident(g41,g6)
    c: Coincident(g41,g0)
    c: Vertical(g41)
    c: Coincident(g42,g28)
    c: PointOnObject(g42,g18)
    c: Horizontal(g42)
    c: Equal(g42,g24)
    c: DistanceX(g19,g19) = 47
FEATURE [PartDesign::Pad] Pad032
  Direction = (1,-2e-16,3e-16)
  Length = 3
  Length2 = 10
  Placement = pos=(0,0,0) rot=(0.57735,0.57735,0.57735;2.0944rad)
  Profile = -> Sketch049
  ReferenceAxis = -> Sketch049 [N_Axis]
  Type = 0
FEATURE [Sketcher::SketchObject] Sketch051
  ExternalGeometry = -> [Sketch049]
  FullyConstrained = true
  MapMode = 5
  Support = -> [XY_Plane012]
  expr: Constraints[10] = <<Spreadsheet>>.NutR
  expr: Constraints[21] = <<Spreadsheet>>.NutR
  expr: Constraints[3] = <<Spreadsheet>>.ScrewD
  sketch-geometry (9):
    g0: LineSegment StartX=1.04e-14 StartY=47 StartZ=0 EndX=-1.1e-15 EndY=-5 EndZ=0
    g1: Circle CenterX=8 CenterY=5 CenterZ=0 NormalX=0 NormalY=0 NormalZ=1 AngleXU=0 Radius=2.1
    g2: Circle CenterX=8 CenterY=37 CenterZ=0 NormalX=0 NormalY=0 NormalZ=1 AngleXU=0 Radius=2.1
    g3: LineSegment StartX=1.04e-14 StartY=47 StartZ=0 EndX=3 EndY=47 EndZ=0
    g4: LineSegment StartX=-1.1e-15 StartY=-5 StartZ=0 EndX=3 EndY=-5 EndZ=0
    g5: ArcOfCircle CenterX=3 CenterY=5 CenterZ=0 NormalX=0 NormalY=0 NormalZ=1 AngleXU=0 Radius=10 StartAngle=4.71239 EndAngle=6.28319
    g6: ArcOfCircle CenterX=3 CenterY=37 CenterZ=0 NormalX=0 NormalY=0 NormalZ=1 AngleXU=0 Radius=10 StartAngle=0 EndAngle=1.5708
    g7: LineSegment StartX=8 StartY=5 StartZ=0 EndX=8 EndY=37 EndZ=0
    g8: LineSegment StartX=13 StartY=37 StartZ=0 EndX=13 EndY=5 EndZ=0
  constraints (22):
    c: Coincident(g0,g-3)
    c: Coincident(g0,g-3)
    c: Equal(g2,g1)
    c: Diameter(g1) = 4.2
    c: Coincident(g3,g0)
    c: Horizontal(g3)
    c: Coincident(g4,g0)
    c: Horizontal(g4)
    c: Equal(g4,g3)
    c: DistanceX(g4,g4) = 3
    c: DistanceX(g4,g1) = 5
    c: Tangent(g6,g3) = 1.5708
    c: Tangent(g5,g4) = -1.5708
    c: Coincident(g7,g1)
    c: Coincident(g7,g2)
    c: Vertical(g7)
    c: Vertical(g8)
    c: Tangent(g5,g8) = 1.5708
    c: Tangent(g8,g6) = 1.5708
    c: Horizontal(g1,g5)
    c: Horizontal(g2,g6)
    c: DistanceX(g1,g5) = 5
FEATURE [PartDesign::Pad] Pad034
  BaseFeature = -> Pad032
  Direction = (0,0,1)
  Length = 3
  Length2 = 10
  Placement = pos=(0,0,0) rot=(0.57735,0.57735,0.57735;2.0944rad)
  Profile = -> Sketch051
  ReferenceAxis = -> Sketch051 [N_Axis]
  Type = 0
FEATURE [Sketcher::SketchObject] Sketch052
  ExternalGeometry = -> [Sketch049]
  FullyConstrained = true
  MapMode = 5
  Placement = pos=(0,0,0) rot=(0.57735,0.57735,0.57735;2.0944rad)
  Support = -> [YZ_Plane012]
  sketch-geometry (8):
    g0: Circle CenterX=2 CenterY=25.2 CenterZ=0 NormalX=0 NormalY=0 NormalZ=1 AngleXU=0 Radius=1.1
    g1: Circle CenterX=2 CenterY=13.8 CenterZ=0 NormalX=0 NormalY=0 NormalZ=1 AngleXU=0 Radius=1.1
    g2: Circle CenterX=49 CenterY=13.8 CenterZ=0 NormalX=0 NormalY=0 NormalZ=1 AngleXU=0 Radius=1.1
    g3: Circle CenterX=49 CenterY=25.2 CenterZ=0 NormalX=0 NormalY=0 NormalZ=1 AngleXU=0 Radius=1.1
    g4: Circle CenterX=2 CenterY=25.2 CenterZ=0 NormalX=0 NormalY=0 NormalZ=1 AngleXU=0 Radius=2
    g5: Circle CenterX=2 CenterY=13.8 CenterZ=0 NormalX=0 NormalY=0 NormalZ=1 AngleXU=0 Radius=2
    g6: Circle CenterX=49 CenterY=25.2 CenterZ=0 NormalX=0 NormalY=0 NormalZ=1 AngleXU=0 Radius=2
    g7: Circle CenterX=49 CenterY=13.8 CenterZ=0 NormalX=0 NormalY=0 NormalZ=1 AngleXU=0 Radius=2
  constraints (16):
    c: Equal(g-3,g0)
    c: Equal(g-5,g1)
    c: Equal(g2,g-6)
    c: Equal(g3,g-7)
    c: Coincident(g3,g-7)
    c: Coincident(g2,g-6)
    c: Coincident(g1,g-5)
    c: Coincident(g0,g-4)
    c: Coincident(g4,g0)
    c: PointOnObject(g-4,g4)
    c: Coincident(g5,g1)
    c: Coincident(g6,g3)
    c: Coincident(g7,g2)
    c: Equal(g5,g6)
    c: Equal(g6,g7)
    c: Equal(g7,g4)
FEATURE [PartDesign::Pad] Pad035
  BaseFeature = -> Pad034
  Direction = (1,-2e-16,3e-16)
  Length = 5
  Length2 = 10
  Placement = pos=(0,0,0) rot=(0.57735,0.57735,0.57735;2.0944rad)
  Profile = -> Sketch052
  ReferenceAxis = -> Sketch052 [N_Axis]
  Type = 0
FEATURE [PartDesign::Body] Body010  label="PicoBase"
  Group = -> [Sketch049,Pad032,Sketch051,Pad034,Sketch052,Pad035]
  Origin = -> Origin012
  Placement = pos=(122,0,5) rot=(0,0,1;0rad)
  Tip = -> Pad035
  expr: .Placement.Base.z = <<InnerIndexArch>>.Placement.Base.z
COMPONENT P10 — recipe-attached ("PicoStandoffs001", modeled in this document).
Construction recipe (the document's own serialized feature program — sketch geometry with constraints, then the solid features built on it; lengths are millimeters unless a unit is written):

FEATURE [Sketcher::SketchObject] Sketch053
  FullyConstrained = true
  MapMode = 5
  Placement = pos=(0,0,0) rot=(0.57735,0.57735,0.57735;2.0944rad)
  Support = -> [YZ_Plane013]
  sketch-geometry (2):
    g0: Circle CenterX=0 CenterY=0 CenterZ=0 NormalX=0 NormalY=0 NormalZ=1 AngleXU=0 Radius=1.05
    g1: Circle CenterX=0 CenterY=0 CenterZ=0 NormalX=0 NormalY=0 NormalZ=1 AngleXU=0 Radius=1.9
  constraints (4):
    c: Coincident(g0,g-1)
    c: Coincident(g1,g0)
    c: Diameter(g0) = 2.1
    c: Diameter(g1) = 3.8
FEATURE [PartDesign::Pad] Pad036
  Direction = (1,-2e-16,3e-16)
  Length = 3
  Length2 = 10
  Placement = pos=(0,0,0) rot=(0.57735,0.57735,0.57735;2.0944rad)
  Profile = -> Sketch053
  ReferenceAxis = -> Sketch053 [N_Axis]
  Type = 0
FEATURE [PartDesign::Body] Body011  label="PicoStandoffs"
  Group = -> [Sketch053,Pad036]
  Origin = -> Origin013
  Placement = pos=(129,2,30) rot=(0,0,1;0rad)
  Tip = -> Pad036
COMPONENT P11 — same part as P10; its construction recipe is shown at P10.
COMPONENT P12 — same part as P10; its construction recipe is shown at P10.
COMPONENT P13 — geometry summary ("PICO"; no construction recipe available for this part):
  bounding box: 52.3 x 21.0 x 3.7 mm
  tessellated surface: 23,136 triangles
  volume: 1145 mm^3 (28% of its bounding box)
COMPONENT P14 — recipe-attached ("Tenting Part", modeled in this document).
Construction recipe (the document's own serialized feature program — sketch geometry with constraints, then the solid features built on it; lengths are millimeters unless a unit is written):

FEATURE [Sketcher::SketchObject] Sketch054
  FullyConstrained = true
  MapMode = 5
  Placement = pos=(0,0,0) rot=(1,0,0;1.5708rad)
  Support = -> [XZ_Plane015]
  expr: .Constraints.real = <<InnerIndexArch>>.Placement.Base.z - 3mm
  expr: Constraints[11] = 10mm - <<Spreadsheet>>.NutR
  expr: Constraints[26] = <<Spreadsheet>>.Wiring
  expr: Constraints[28] = <<Spreadsheet>>.NutR * 6
  expr: Constraints[8] = 40mm + <<Spreadsheet>>.NutR * 2
  sketch-geometry (10):
    g0: LineSegment StartX=-55 StartY=-1 StartZ=0 EndX=-5 EndY=-1 EndZ=0
    g1: LineSegment StartX=-5 StartY=-1 StartZ=0 EndX=-5 EndY=2 EndZ=0
    g2: LineSegment StartX=-5 StartY=2 StartZ=0 EndX=-55 EndY=2 EndZ=0
    g3: LineSegment StartX=-55 StartY=2 StartZ=0 EndX=-55 EndY=-1 EndZ=0
    g4: LineSegment StartX=4 StartY=-1 StartZ=0 EndX=4 EndY=2 EndZ=0
    g5: LineSegment StartX=4 StartY=2 StartZ=0 EndX=-5 EndY=2 EndZ=0
    g6: LineSegment StartX=-5 StartY=-1 StartZ=0 EndX=1 EndY=-1 EndZ=0
    g7: LineSegment StartX=1 StartY=-1 StartZ=0 EndX=1 EndY=-31 EndZ=0
    g8: LineSegment StartX=1 StartY=-31 StartZ=0 EndX=4 EndY=-31 EndZ=0
    g9: LineSegment StartX=4 StartY=-1 StartZ=0 EndX=4 EndY=-31 EndZ=0
  constraints (29):
    c: Coincident(g0,g1)
    c: Coincident(g1,g2)
    c: Coincident(g2,g3)
    c: Coincident(g3,g0)
    c: Horizontal(g0)
    c: Horizontal(g2)
    c: Vertical(g1)
    c: Vertical(g3)
    c: DistanceX(g2,g2) = 50
    c: DistanceY(g-1,g1) = 2  'real'
    c: DistanceY(g1,g1) = 3
    c: DistanceX(g1,g-1) = 5
    c: Vertical(g4)
    c: Coincident(g4,g5)
    c: Coincident(g5,g2)
    c: Horizontal(g5)
    c: Coincident(g6,g0)
    c: Horizontal(g6)
    c: Coincident(g6,g7)
    c: Vertical(g7)
    c: Coincident(g7,g8)
    c: Horizontal(g8)
    c: Coincident(g9,g8)
    c: Vertical(g9)
    c: PointOnObject(g4,g6)
    c: Equal(g8,g1)
    c: DistanceX(g6,g6) = 6
    c: Coincident(g4,g9)
    c: DistanceY(g9,g9) = 30
FEATURE [PartDesign::Pad] Pad037
  Direction = (0,-1,-2e-16)
  Length = 46
  Length2 = 3
  Placement = pos=(0,0,0) rot=(1,0,0;1.5708rad)
  Profile = -> Sketch054
  ReferenceAxis = -> Sketch054 [N_Axis]
  Type = 4
  expr: Length = <<Spreadsheet>>.NutR * 2 * 4 + <<Spreadsheet>>.Wiring
FEATURE [Sketcher::SketchObject] Sketch055
  ExternalGeometry = -> [Sketch054]
  FullyConstrained = true
  MapMode = 5
  Placement = pos=(0,0,0) rot=(1,0,0;1.5708rad)
  Support = -> [XZ_Plane015]
  expr: Constraints[11] = Spreadsheet.NutR
  expr: Constraints[15] = <<Spreadsheet>>.NutR * 2
  expr: Constraints[19] = <<Spreadsheet>>.ScrewD
  sketch-geometry (32):
    g0: ArcOfCircle CenterX=9 CenterY=-28.2857 CenterZ=0 NormalX=0 NormalY=0 NormalZ=1 AngleXU=0 Radius=2.1 StartAngle=3.14159 EndAngle=6.28319
    g1: LineSegment StartX=6.9 StartY=-8 StartZ=0 EndX=6.9 EndY=-28.2857 EndZ=0
    g2: LineSegment StartX=11.1 StartY=-28.2857 StartZ=0 EndX=11.1 EndY=-8 EndZ=0
    g3: ArcOfCircle CenterX=9 CenterY=-38.2857 CenterZ=0 NormalX=0 NormalY=0 NormalZ=1 AngleXU=0 Radius=2.1 StartAngle=4.71239 EndAngle=7.85398
    g4: ArcOfCircle CenterX=-8.44423 CenterY=-28.2143 CenterZ=0 NormalX=0 NormalY=0 NormalZ=1 AngleXU=0 Radius=2.1 StartAngle=0.523599 EndAngle=3.66519
    g5: ArcOfCircle CenterX=9 CenterY=-38.2857 CenterZ=0 NormalX=0 NormalY=0 NormalZ=1 AngleXU=0 Radius=5 StartAngle=4.71239 EndAngle=6.47156
    g6: ArcOfCircle CenterX=-8.44423 CenterY=-28.2143 CenterZ=0 NormalX=0 NormalY=0 NormalZ=1 AngleXU=0 Radius=5 StartAngle=2.16569 EndAngle=3.66519
    g7: ArcOfCircle CenterX=-26.8593 CenterY=-1 CenterZ=0 NormalX=0 NormalY=0 NormalZ=1 AngleXU=0 Radius=27.8593 StartAngle=5.30728 EndAngle=6.28319
    g8: LineSegment StartX=4 StartY=2 StartZ=0 EndX=1 EndY=-1 EndZ=0
    g9: LineSegment StartX=-8.44423 StartY=-28.2143 StartZ=0 EndX=-12.7744 EndY=-30.7143 EndZ=0
    g10: LineSegment StartX=9 StartY=-38.2857 StartZ=0 EndX=9 EndY=-43.2857 EndZ=0
    g11: LineSegment StartX=-1.64151 StartY=-35.2453 StartZ=0 EndX=1 EndY=-31 EndZ=0
    g12: LineSegment StartX=9 StartY=-28.2857 StartZ=0 EndX=9 EndY=-38.2857 EndZ=0
    g13: ArcOfCircle CenterX=9 CenterY=-8 CenterZ=0 NormalX=0 NormalY=0 NormalZ=1 AngleXU=0 Radius=2.1 StartAngle=0 EndAngle=3.14159
    g14: ArcOfCircle CenterX=9 CenterY=2 CenterZ=0 NormalX=0 NormalY=0 NormalZ=1 AngleXU=0 Radius=2.1 StartAngle=1.5708 EndAngle=4.71239
    g15: ArcOfCircle CenterX=26.4442 CenterY=-8.07143 CenterZ=0 NormalX=0 NormalY=0 NormalZ=1 AngleXU=0 Radius=2.1 StartAngle=3.66519 EndAngle=6.80678
    g16: LineSegment StartX=9 StartY=2 StartZ=0 EndX=9 EndY=-8 EndZ=0
    g17: LineSegment StartX=26.4442 StartY=-8.07143 StartZ=0 EndX=24.6256 EndY=-9.12143 EndZ=0
    g18: ArcOfCircle CenterX=35.2282 CenterY=-33.2857 CenterZ=0 NormalX=0 NormalY=0 NormalZ=1 AngleXU=0 Radius=21.7005 StartAngle=1.90602 EndAngle=3.32997
    g19: ArcOfCircle CenterX=26.4442 CenterY=-8.07143 CenterZ=0 NormalX=0 NormalY=0 NormalZ=1 AngleXU=0 Radius=5 StartAngle=5.04761 EndAngle=6.80678
    g20: LineSegment StartX=26.4442 StartY=-8.07143 StartZ=0 EndX=31.4442 EndY=-8.07143 EndZ=0
    g21: LineSegment StartX=9 StartY=-28.2857 StartZ=0 EndX=13.9115 EndY=-29.222 EndZ=0
    g22: ArcOfCircle CenterX=9 CenterY=2 CenterZ=0 NormalX=0 NormalY=0 NormalZ=1 AngleXU=0 Radius=5 StartAngle=1.5708 EndAngle=3.14159
    g23: ArcOfCircle CenterX=9 CenterY=-18.1429 CenterZ=0 NormalX=0 NormalY=0 NormalZ=1 AngleXU=0 Radius=18.0429 StartAngle=3.66519 EndAngle=4.71239
    g24: ArcOfCircle CenterX=9 CenterY=-18.1429 CenterZ=0 NormalX=0 NormalY=0 NormalZ=1 AngleXU=0 Radius=22.2429 StartAngle=3.66519 EndAngle=4.71239
    g25: ArcOfCircle CenterX=9 CenterY=-18.1429 CenterZ=0 NormalX=0 NormalY=0 NormalZ=1 AngleXU=0 Radius=25.1429 StartAngle=3.66519 EndAngle=4.71239
    g26: ArcOfCircle CenterX=9 CenterY=-18.1429 CenterZ=0 NormalX=0 NormalY=0 NormalZ=1 AngleXU=0 Radius=18.0429 StartAngle=0.523599 EndAngle=1.5708
    g27: ArcOfCircle CenterX=9 CenterY=-18.1429 CenterZ=0 NormalX=0 NormalY=0 NormalZ=1 AngleXU=0 Radius=22.2429 StartAngle=0.523599 EndAngle=1.5708
    g28: ArcOfCircle CenterX=9 CenterY=-18.1429 CenterZ=0 NormalX=0 NormalY=0 NormalZ=1 AngleXU=0 Radius=25.1429 StartAngle=0.523599 EndAngle=1.5708
    g29: ArcOfCircle CenterX=9 CenterY=-18.1429 CenterZ=0 NormalX=0 NormalY=0 NormalZ=1 AngleXU=0 Radius=20.1429 StartAngle=3.66519 EndAngle=4.71239
    g30: LineSegment StartX=-6.62557 StartY=-27.1643 StartZ=0 EndX=9 EndY=-18.1429 EndZ=0
    g31: LineSegment StartX=9 StartY=-18.1429 StartZ=0 EndX=24.6256 EndY=-9.12143 EndZ=0
  constraints (78):
    c: Tangent(g1,g0) = -1.5708
    c: Tangent(g0,g2) = -1.5708
    c: Vertical(g1)
    c: Coincident(g5,g3)
    c: Coincident(g6,g4)
    c: Equal(g3,g0)
    c: Coincident(g6,g9) = -1.5708
    c: Tangent(g7,g6) = 1.5708
    c: Coincident(g9,g4)
    c: Coincident(g10,g3)
    c: Coincident(g10,g5)
    c: Distance(g9) = 5
    c: Angle(g9,g10) = 1.0472
    c: Coincident(g12,g0)
    c: Coincident(g12,g3)
    c: Distance(g12) = 10
    c: Vertical(g2)
    c: Tangent(g13,g1) = -1.5708
    c: Tangent(g13,g2) = -1.5708
    c: DistanceX(g1,g2) = 4.2
    c: Coincident(g16,g14)
    c: Coincident(g16,g13)
    c: Equal(g16,g12)
    c: Coincident(g17,g15)
    c: Vertical(g16)
    c: Equal(g14,g13)
    c: Coincident(g15,g17) = 1.5708
    c: Angle(g17,g16) = 1.0472
    c: Tangent(g19,g18) = 1.5708
    c: Coincident(g20,g15)
    c: Horizontal(g20)
    c: Coincident(g19,g15)
    c: Tangent(g18,g5) = 1.5708
    c: Coincident(g21,g0)
    c: PointOnObject(g21,g18)
    c: Perpendicular(g18,g21)
    c: Coincident(g22,g14)
    c: Equal(g11,g9)
    c: Equal(g21,g9)
    c: Coincident(g24,g23)
    c: Tangent(g23,g4) = 1.5708
    c: Tangent(g23,g3) = 1.5708
    c: Tangent(g24,g3) = -1.5708
    c: Tangent(g24,g4) = -1.5708
    c: PointOnObject(g3,g10)
    c: PointOnObject(g4,g9)
    c: Coincident(g25,g23)
    c: Coincident(g25,g5)
    c: Coincident(g25,g6)
    c: Coincident(g26,g23)
    c: Tangent(g26,g14) = 1.5708
    c: Tangent(g26,g15) = 1.5708
    c: Coincident(g27,g23)
    c: Tangent(g27,g15) = -1.5708
    c: Tangent(g27,g14) = -1.5708
    c: Equal(g20,g21)
    c: Coincident(g22,g8)
    c: Coincident(g28,g23)
    c: Tangent(g28,g22) = -1.5708
    c: Tangent(g28,g19) = -1.5708
    c: PointOnObject(g14,g16)
    c: Coincident(g29,g4)
    c: Coincident(g29,g3)
    c: Perpendicular(g29,g11)
    c: Perpendicular(g29,g9)
    c: Coincident(g4,g30)
    c: Coincident(g30,g31)
    c: Coincident(g31,g15)
    c: Coincident(g23,g30)
    c: Equal(g31,g30)
    c: PointOnObject(g20,g19)
    c: PointOnObject(g11,g29)
    c: Vertical(g12)
    c: Coincident(g11,g-5)
    c: Coincident(g8,g-4)
    c: Tangent(g7,g-3) = 1.5708
    c: Coincident(g8,g7)
    c: Horizontal(g8,g14)
FEATURE [PartDesign::Pad] Pad038
  BaseFeature = -> Pad037
  Direction = (0,-1,-2e-16)
  Length = 3
  Length2 = 10
  Placement = pos=(0,0,0) rot=(1,0,0;1.5708rad)
  Profile = -> Sketch055
  ReferenceAxis = -> Sketch055 [N_Axis]
  Reversed = true
  Type = 0
FEATURE [Sketcher::SketchObject] Sketch060
  FullyConstrained = true
  MapMode = 5
  Placement = pos=(0,0,0) rot=(1,0,0;1.5708rad)
  Support = -> [XZ_Plane016]
  expr: Constraints[11] = <<Spreadsheet>>.NutR + 3mm
  expr: Constraints[32] = <<Spreadsheet>>.NutR * 2
  expr: Constraints[39] = <<Spreadsheet>>.NutR
  expr: Constraints[41] = <<Spreadsheet>>.ScrewD / 2
  expr: Constraints[42] = <<Spreadsheet>>.NutR
  expr: Constraints[48] = <<Spreadsheet>>.NutR * 9
  sketch-geometry (23):
    g0: ArcOfCircle CenterX=14.6985 CenterY=-1.7101 CenterZ=0 NormalX=0 NormalY=0 NormalZ=1 AngleXU=0 Radius=2.1 StartAngle=5.93412 EndAngle=9.07571
    g1: ArcOfCircle CenterX=-16.0661 CenterY=-27.759 CenterZ=0 NormalX=0 NormalY=0 NormalZ=1 AngleXU=0 Radius=15 StartAngle=4.36332 EndAngle=5.93412
    g2: ArcOfCircle CenterX=14.6985 CenterY=-1.7101 CenterZ=0 NormalX=0 NormalY=0 NormalZ=1 AngleXU=0 Radius=5 StartAngle=0.000890861 EndAngle=2.79253
    g3: LineSegment StartX=-21.1964 StartY=-41.8544 StartZ=0 EndX=-32.4727 EndY=-37.7501 EndZ=0
    g4: LineSegment StartX=-32.4727 StartY=-37.7501 StartZ=0 EndX=-34.1828 EndY=-42.4486 EndZ=0
    g5: LineSegment StartX=-34.1828 StartY=-42.4486 StartZ=0 EndX=3.40488 EndY=-56.1294 EndZ=0
    g6: LineSegment StartX=19.6985 StartY=-1.70565 StartZ=0 EndX=19.7058 EndY=-9.92528 EndZ=0
    g7: ArcOfCircle CenterX=11.7058 CenterY=-9.93241 CenterZ=0 NormalX=0 NormalY=0 NormalZ=1 AngleXU=0 Radius=8 StartAngle=5.93412 EndAngle=6.28408
    g8: LineSegment StartX=8.71311 StartY=-18.1547 StartZ=0 EndX=16.2307 EndY=-20.8909 EndZ=0
    g9: LineSegment StartX=19.2233 StartY=-12.6686 StartZ=0 EndX=3.40488 EndY=-56.1294 EndZ=0
    g10: LineSegment StartX=-1.97072 StartY=-32.8893 StartZ=0 EndX=10 EndY=0 EndZ=0
    g11: ArcOfCircle CenterX=5.2929 CenterY=-27.5516 CenterZ=0 NormalX=0 NormalY=0 NormalZ=1 AngleXU=0 Radius=2.1 StartAngle=5.93412 EndAngle=9.07571
    g12: ArcOfCircle CenterX=-0.692466 CenterY=-43.9963 CenterZ=0 NormalX=0 NormalY=0 NormalZ=1 AngleXU=0 Radius=2.1 StartAngle=2.79253 EndAngle=5.93412
    g13: LineSegment StartX=3.31955 StartY=-26.8334 StartZ=0 EndX=-2.66582 EndY=-43.278 EndZ=0
    g14: LineSegment StartX=1.28089 StartY=-44.7145 StartZ=0 EndX=7.26625 EndY=-28.2699 EndZ=0
    g15: LineSegment StartX=12.7251 StartY=-0.991858 StartZ=0 EndX=6.73976 EndY=-17.4365 EndZ=0
    g16: LineSegment StartX=10.6865 StartY=-18.873 StartZ=0 EndX=16.6718 EndY=-2.42834 EndZ=0
    g17: ArcOfCircle CenterX=8.71311 CenterY=-18.1547 CenterZ=0 NormalX=0 NormalY=0 NormalZ=1 AngleXU=0 Radius=2.1 StartAngle=2.79253 EndAngle=5.93412
    g18: LineSegment StartX=-21.1964 StartY=-41.8544 StartZ=0 EndX=-2.40256 EndY=-48.6947 EndZ=0
    g19: LineSegment StartX=-0.692466 StartY=-43.9963 StartZ=0 EndX=-2.40256 EndY=-48.6947 EndZ=0
    g20: LineSegment StartX=6.73976 StartY=-17.4365 StartZ=0 EndX=3.31955 EndY=-26.8334 EndZ=0
    g21: LineSegment StartX=14.6985 StartY=-1.7101 StartZ=0 EndX=11.7058 EndY=-9.93241 EndZ=0
    g22: LineSegment StartX=11.7058 StartY=-9.93241 StartZ=0 EndX=8.71311 EndY=-18.1547 EndZ=0
  constraints (57):
    c: Coincident(g2,g0)
    c: Tangent(g1,g3) = 1.5708
    c: Coincident(g3,g4)
    c: Coincident(g4,g5)
    c: Perpendicular(g3,g4)
    c: Perpendicular(g5,g4)
    c: Distance(g4) = 5
    c: Tangent(g6,g2) = 1.5708
    c: Radius(g1) = 15
    c: Angle(g3,g-1) = 0.349066
    c: Distance(g5) = 40
    c: Distance(g8) = 8
    c: Tangent(g7,g6) = 1.5708
    c: Coincident(g9,g5)
    c: Tangent(g10,g1) = -1.5708
    c: Perpendicular(g5,g9)
    c: Parallel(g10,g9)
    c: PointOnObject(g8,g9)
    c: Perpendicular(g9,g8)
    c: Tangent(g11,g13) = -1.5708
    c: Tangent(g13,g12) = -1.5708
    c: Tangent(g12,g14) = -1.5708
    c: Tangent(g14,g11) = -1.5708
    c: Equal(g11,g12)
    c: Tangent(g15,g0) = -1.5708
    c: Tangent(g16,g0) = -1.5708
    c: Tangent(g17,g16) = -1.5708
    c: Tangent(g17,g15) = -1.5708
    c: Parallel(g16,g9)
    c: Parallel(g16,g15)
    c: Tangent(g10,g2) = 1.5708
    c: Equal(g11,g17)
    c: Distance(g17,g11) = 10
    c: Equal(g15,g13)
    c: Tangent(g9,g7) = 1.5708
    c: Coincident(g18,g1)
    c: Tangent(g18,g1)
    c: Coincident(g19,g12)
    c: Coincident(g19,g18)
    c: Distance(g19) = 5
    c: Perpendicular(g18,g19)
    c: Radius(g0) = 2.1
    c: Distance(g0,g2) = 5
    c: Coincident(g20,g15)
    c: Tangent(g20,g17)
    c: Parallel(g13,g20)
    c: Coincident(g11,g20)
    c: Coincident(g8,g17)
    c: Distance(g0,g12) = 45
    c: Coincident(g21,g0)
    c: Coincident(g21,g7)
    c: Coincident(g22,g7)
    c: Coincident(g22,g17)
    c: Equal(g21,g22)
    c: Angle(g21,g22) = 3.14159
    c: DistanceX(g-1,g2) = 10
    c: PointOnObject(g2,g-1)
FEATURE [PartDesign::Pad] Pad039
  Direction = (0,-1,-2e-16)
  Length = 4
  Length2 = 10
  Placement = pos=(0,0,0) rot=(1,0,0;1.5708rad)
  Profile = -> Sketch060
  ReferenceAxis = -> Sketch060 [N_Axis]
  Type = 0
FEATURE [Sketcher::SketchObject] Sketch061
  ExternalGeometry = -> [Sketch060]
  FullyConstrained = true
  MapMode = 5
  Placement = pos=(0,0,0) rot=(1,0,0;1.5708rad)
  Support = -> [XZ_Plane016]
  sketch-geometry (4):
    g0: LineSegment StartX=5.11498 StartY=-51.4309 StartZ=0 EndX=-32.4727 EndY=-37.7501 EndZ=0
    g1: LineSegment StartX=-32.4727 StartY=-37.7501 StartZ=0 EndX=-34.1828 EndY=-42.4486 EndZ=0
    g2: LineSegment StartX=-34.1828 StartY=-42.4486 StartZ=0 EndX=3.40488 EndY=-56.1294 EndZ=0
    g3: LineSegment StartX=5.11498 StartY=-51.4309 StartZ=0 EndX=3.40488 EndY=-56.1294 EndZ=0
  constraints (9):
    c: Coincident(g0,g1)
    c: Coincident(g1,g2)
    c: Coincident(g1,g-3)
    c: Coincident(g0,g-3)
    c: Coincident(g3,g0)
    c: Coincident(g3,g2)
    c: PointOnObject(g-5,g0)
    c: Coincident(g2,g-4)
    c: PointOnObject(g0,g-4)
FEATURE [PartDesign::Pad] Pad040
  BaseFeature = -> Pad039
  Direction = (0,-1,-2e-16)
  Length = 20
  Length2 = 10
  Placement = pos=(0,0,0) rot=(1,0,0;1.5708rad)
  Profile = -> Sketch061
  ReferenceAxis = -> Sketch061 [N_Axis]
  Reversed = true
  Type = 0
FEATURE [PartDesign::Body] Body013  label="TentingFoot"
  Group = -> [Sketch060,Pad039,Sketch061,Pad040]
  Origin = -> Origin016
  Placement = pos=(140,55,0) rot=(0,0,1;0rad)
  Tip = -> Pad040
FEATURE [Sketcher::SketchObject] Sketch056
  ExternalGeometry = -> [Pad038]
  FullyConstrained = true
  MapMode = 5
  Support = -> [XY_Plane015]
  expr: Constraints[18] = <<Spreadsheet>>.ScrewD
  expr: Constraints[42] = <<Spreadsheet>>.NutR
  sketch-geometry (18):
    g0: ArcOfCircle CenterX=-50 CenterY=-2 CenterZ=0 NormalX=0 NormalY=0 NormalZ=1 AngleXU=0 Radius=2.1 StartAngle=5.53e-14 EndAngle=3.14159
    g1: ArcOfCircle CenterX=-50 CenterY=-41 CenterZ=0 NormalX=0 NormalY=0 NormalZ=1 AngleXU=0 Radius=2.1 StartAngle=3.14159 EndAngle=6.28319
    g2: LineSegment StartX=-52.1 StartY=-2 StartZ=0 EndX=-52.1 EndY=-41 EndZ=0
    g3: LineSegment StartX=-47.9 StartY=-41 StartZ=0 EndX=-47.9 EndY=-2 EndZ=0
    g4: ArcOfCircle CenterX=-30 CenterY=-2 CenterZ=0 NormalX=0 NormalY=0 NormalZ=1 AngleXU=0 Radius=2.1 StartAngle=5.53e-14 EndAngle=3.14159
    g5: ArcOfCircle CenterX=-30 CenterY=-41 CenterZ=0 NormalX=0 NormalY=0 NormalZ=1 AngleXU=0 Radius=2.1 StartAngle=3.14159 EndAngle=6.28319
    g6: LineSegment StartX=-32.1 StartY=-2 StartZ=0 EndX=-32.1 EndY=-41 EndZ=0
    g7: LineSegment StartX=-27.9 StartY=-41 StartZ=0 EndX=-27.9 EndY=-2 EndZ=0
    g8: ArcOfCircle CenterX=-10 CenterY=-2 CenterZ=0 NormalX=0 NormalY=0 NormalZ=1 AngleXU=0 Radius=2.1 StartAngle=5.31e-14 EndAngle=3.14159
    g9: ArcOfCircle CenterX=-10 CenterY=-41 CenterZ=0 NormalX=0 NormalY=0 NormalZ=1 AngleXU=0 Radius=2.1 StartAngle=3.14159 EndAngle=6.28319
    g10: LineSegment StartX=-12.1 StartY=-2 StartZ=0 EndX=-12.1 EndY=-41 EndZ=0
    g11: LineSegment StartX=-7.9 StartY=-41 StartZ=0 EndX=-7.9 EndY=-2 EndZ=0
    g12: LineSegment StartX=-50 StartY=-2 StartZ=0 EndX=-30 EndY=-2 EndZ=0
    g13: LineSegment StartX=-30 StartY=-2 StartZ=0 EndX=-10 EndY=-2 EndZ=0
    g14: LineSegment StartX=-10 StartY=-41 StartZ=0 EndX=-30 EndY=-41 EndZ=0
    g15: LineSegment StartX=-30 StartY=-41 StartZ=0 EndX=-50 EndY=-41 EndZ=0
    g16: LineSegment StartX=-50 StartY=-41 StartZ=0 EndX=-50 EndY=-46 EndZ=0
    g17: LineSegment StartX=-50 StartY=-2 StartZ=0 EndX=-50 EndY=3 EndZ=0
  constraints (44):
    c: Tangent(g0,g2) = -1.5708
    c: Tangent(g2,g1) = -1.5708
    c: Tangent(g1,g3) = -1.5708
    c: Tangent(g3,g0) = -1.5708
    c: Equal(g0,g1)
    c: Vertical(g2)
    c: Tangent(g4,g6) = -1.5708
    c: Tangent(g6,g5) = -1.5708
    c: Tangent(g5,g7) = -1.5708
    c: Tangent(g7,g4) = -1.5708
    c: Equal(g4,g5)
    c: Vertical(g6)
    c: Tangent(g8,g10) = -1.5708
    c: Tangent(g10,g9) = -1.5708
    c: Tangent(g9,g11) = -1.5708
    c: Tangent(g11,g8) = -1.5708
    c: Equal(g8,g9)
    c: Vertical(g10)
    c: DistanceX(g9,g9) = 4.2
    c: Equal(g9,g5)
    c: Equal(g5,g1)
    c: Coincident(g12,g0)
    c: Coincident(g12,g4)
    c: Horizontal(g12)
    c: Coincident(g13,g4)
    c: Coincident(g13,g8)
    c: Horizontal(g13)
    c: Coincident(g14,g9)
    c: Coincident(g14,g5)
    c: Horizontal(g14)
    c: Coincident(g14,g15)
    c: Coincident(g15,g1)
    c: Horizontal(g15)
    c: Equal(g15,g14)
    c: DistanceX(g15,g15) = 20
    c: DistanceX(g8,g-1) = 10
    c: Coincident(g16,g1)
    c: Vertical(g16)
    c: Coincident(g17,g0)
    c: PointOnObject(g17,g-3)
    c: Vertical(g17)
    c: Equal(g17,g16)
    c: DistanceY(g16,g16) = 5
    c: PointOnObject(g16,g-4)
FEATURE [PartDesign::Pocket] Pocket016
  BaseFeature = -> Pad038
  Direction = (0,0,-1)
  Length = 20
  Length2 = 5
  Midplane = true
  Placement = pos=(0,0,0) rot=(1,0,0;1.5708rad)
  Profile = -> Sketch056
  ReferenceAxis = -> Sketch056 [N_Axis]
  Type = 0
FEATURE [Sketcher::SketchObject] Sketch066
  ExternalGeometry = -> [Pocket016]
  FullyConstrained = true
  MapMode = 5
  Placement = pos=(4,0,0) rot=(0.707107,0,0.707107;3.14159rad)
  Support = -> [Pocket016]
  expr: Constraints[17] = <<Spreadsheet>>.NutR * 2
  expr: Constraints[18] = <<Spreadsheet>>.NutR * 2
  expr: Constraints[19] = <<Spreadsheet>>.NutR * 6
  expr: Constraints[20] = <<Spreadsheet>>.NutR * 4
  expr: Constraints[21] = <<Spreadsheet>>.NutR * 2
  expr: Constraints[45] = <<Spreadsheet>>.ScrewD
  expr: Constraints[48] = <<Spreadsheet>>.NutR
  expr: Constraints[49] = <<Spreadsheet>>.NutR
  sketch-geometry (19):
    g0: LineSegment StartX=-26 StartY=41 StartZ=0 EndX=-26 EndY=11 EndZ=0
    g1: LineSegment StartX=-16 StartY=11 StartZ=0 EndX=-16 EndY=41 EndZ=0
    g2: LineSegment StartX=-6 StartY=41 StartZ=0 EndX=-6 EndY=11 EndZ=0
    g3: LineSegment StartX=-6 StartY=21 StartZ=0 EndX=-26 EndY=21 EndZ=0
    g4: LineSegment StartX=-26 StartY=31 StartZ=0 EndX=-6 EndY=31 EndZ=0
    g5: LineSegment StartX=-6 StartY=41 StartZ=0 EndX=-26 EndY=41 EndZ=0
    g6: LineSegment StartX=-26 StartY=11 StartZ=0 EndX=-6 EndY=11 EndZ=0
    g7: Circle CenterX=-26 CenterY=41 CenterZ=0 NormalX=0 NormalY=0 NormalZ=1 AngleXU=0 Radius=2.1
    g8: Circle CenterX=-16 CenterY=31 CenterZ=0 NormalX=0 NormalY=0 NormalZ=1 AngleXU=0 Radius=2.1
    g9: Circle CenterX=-16 CenterY=21 CenterZ=0 NormalX=0 NormalY=0 NormalZ=1 AngleXU=0 Radius=2.1
    g10: Circle CenterX=-16 CenterY=41 CenterZ=0 NormalX=0 NormalY=0 NormalZ=1 AngleXU=0 Radius=2.1
    g11: Circle CenterX=-6 CenterY=31 CenterZ=0 NormalX=0 NormalY=0 NormalZ=1 AngleXU=0 Radius=2.1
    g12: Circle CenterX=-6 CenterY=41 CenterZ=0 NormalX=0 NormalY=0 NormalZ=1 AngleXU=0 Radius=2.1
    g13: Circle CenterX=-26 CenterY=31 CenterZ=0 NormalX=0 NormalY=0 NormalZ=1 AngleXU=0 Radius=2.1
    g14: Circle CenterX=-26 CenterY=21 CenterZ=0 NormalX=0 NormalY=0 NormalZ=1 AngleXU=0 Radius=2.1
    g15: Circle CenterX=-26 CenterY=11 CenterZ=0 NormalX=0 NormalY=0 NormalZ=1 AngleXU=0 Radius=2.1
    g16: Circle CenterX=-16 CenterY=11 CenterZ=0 NormalX=0 NormalY=0 NormalZ=1 AngleXU=0 Radius=2.1
    g17: Circle CenterX=-6 CenterY=11 CenterZ=0 NormalX=0 NormalY=0 NormalZ=1 AngleXU=0 Radius=2.1
    g18: Circle CenterX=-6 CenterY=21 CenterZ=0 NormalX=0 NormalY=0 NormalZ=1 AngleXU=0 Radius=2.1
  constraints (50):
    c: Vertical(g0)
    c: Vertical(g1)
    c: Vertical(g2)
    c: PointOnObject(g3,g2)
    c: PointOnObject(g3,g0)
    c: Horizontal(g3)
    c: PointOnObject(g4,g0)
    c: PointOnObject(g4,g2)
    c: Horizontal(g4)
    c: Coincident(g5,g2)
    c: Coincident(g5,g0)
    c: Horizontal(g5)
    c: Coincident(g6,g0)
    c: Coincident(g6,g2)
    c: Horizontal(g6)
    c: PointOnObject(g1,g6)
    c: PointOnObject(g1,g5)
    c: DistanceY(g4,g0) = 10
    c: DistanceY(g3,g4) = 10
    c: DistanceY(g2,g2) = 30
    c: DistanceX(g6,g6) = 20
    c: DistanceX(g0,g1) = 10
    c: Coincident(g7,g0)
    c: PointOnObject(g8,g1)
    c: PointOnObject(g9,g1)
    c: Coincident(g10,g1)
    c: Coincident(g11,g4)
    c: Coincident(g12,g2)
    c: Coincident(g13,g4)
    c: Coincident(g14,g3)
    c: Coincident(g15,g0)
    c: Coincident(g16,g1)
    c: Coincident(g17,g2)
    c: Coincident(g18,g3)
    c: Equal(g13,g7)
    c: Equal(g7,g14)
    c: Equal(g14,g15)
    c: Equal(g15,g16)
    c: Equal(g16,g9)
    c: Equal(g9,g8)
    c: Equal(g8,g10)
    c: Equal(g10,g12)
    c: Equal(g12,g11)
    c: Equal(g11,g18)
    c: Equal(g18,g17)
    c: Diameter(g7) = 4.2
    c: PointOnObject(g8,g4)
    c: PointOnObject(g9,g3)
    c: DistanceX(g-3,g7) = 5
    c: DistanceY(g7,g-3) = 5
FEATURE [PartDesign::Pocket] Pocket023
  BaseFeature = -> Pocket016
  Direction = (-1,0,2e-16)
  Length = 5
  Length2 = 5
  Placement = pos=(0,0,0) rot=(1,0,0;1.5708rad)
  Profile = -> Sketch066
  ReferenceAxis = -> Sketch066 [N_Axis]
  Type = 0
FEATURE [PartDesign::Body] Body012  label="TentingLeg"
  Group = -> [Sketch054,Pad037,Sketch055,Pad038,Sketch056,Pocket016,Sketch066,Pocket023]
  Origin = -> Origin015
  Placement = pos=(140,47,0) rot=(0,0,1;0rad)
  Tip = -> Pocket023
PROVENANCE & LICENSES
A FreeCAD (.FCStd) document from a public repository crawl; recipes are the document's own serialized feature recipes (and, for linked parts, companion documents' recipes).
License: as declared in the source repository (recorded in the dataset sidecar).
